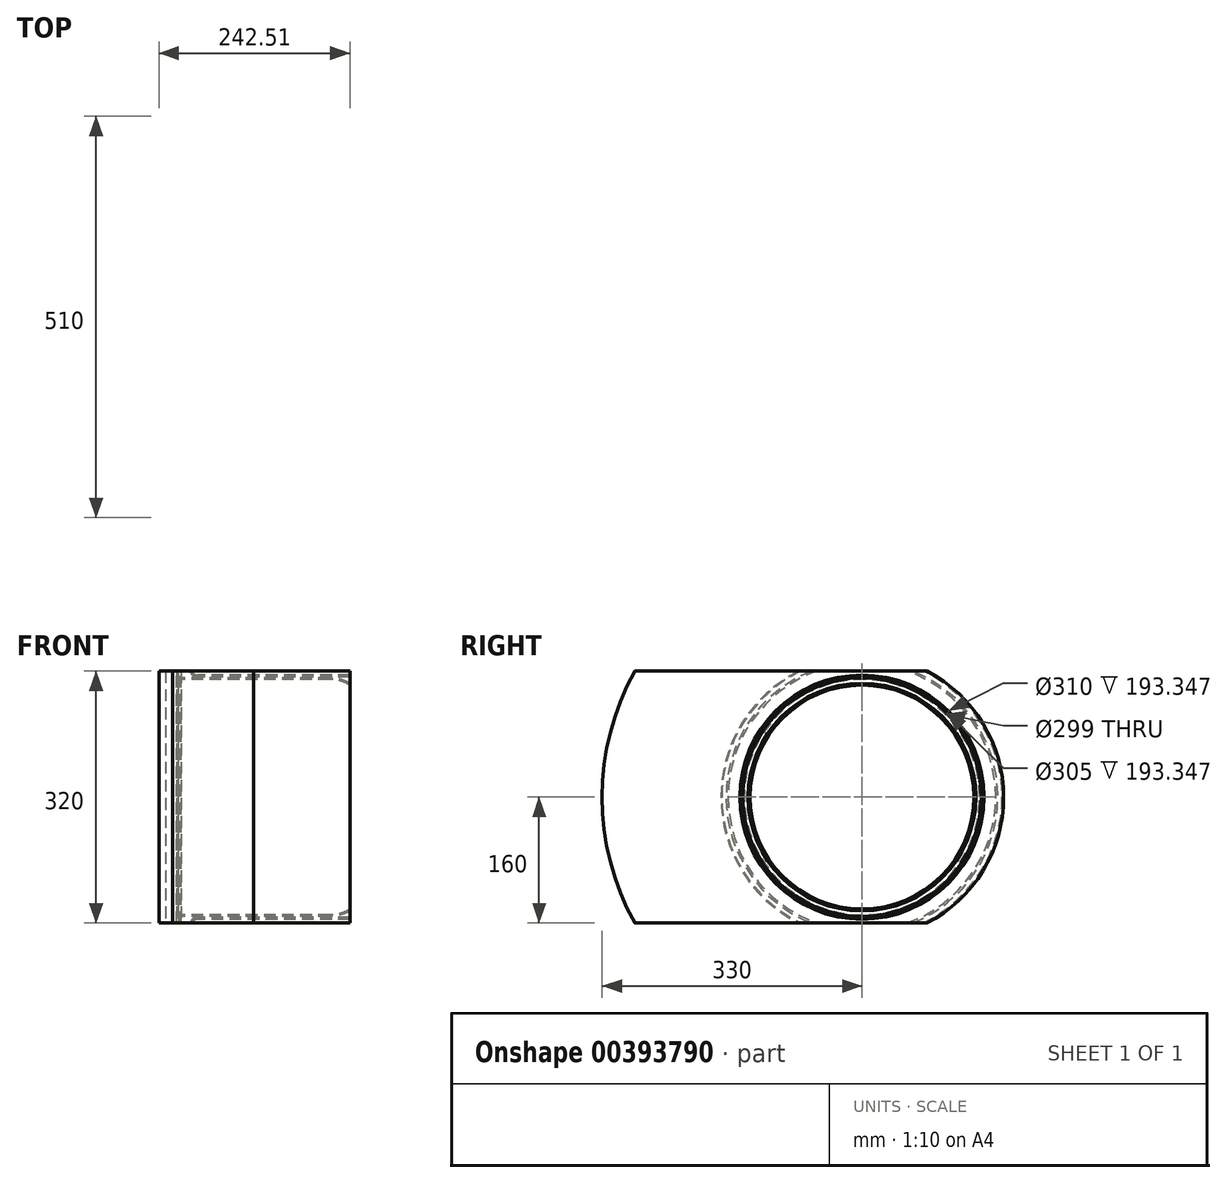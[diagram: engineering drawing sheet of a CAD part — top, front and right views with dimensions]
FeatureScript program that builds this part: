
annotation { "Feature Type Name" : "Feature", "Feature Type Description" : "" }
export const myFeature = defineFeature(function(context is Context, id is Id, definition is map)
    precondition{}
    {
        {
            var Q0;
            Q0=qCreatedBy(makeId("Front.planeOp"),FACE);
            var sketch = newSketch(context, id + "F0", { "sketchPlane" : qUnion([Q0])});
            skLineSegment(sketch, "E0", {"start": v(83.6, 147.98) * mm, "end": v(98.28, 137.71) * mm});
            skLineSegment(sketch, "E1", {"start": v(106.88, 135) * mm, "end": v(107.42, 135) * mm});
            skLineSegment(sketch, "E2", {"start": v(116.02, 137.71) * mm, "end": v(130.7, 147.98) * mm});
            skLineSegment(sketch, "E3", {"start": v(145.03, 152.5) * mm, "end": v(193.35, 152.5) * mm});
            skLineSegment(sketch, "E4", {"start": v(211.47, 170) * mm, "end": v(213.15, 170) * mm});
            skLineSegment(sketch, "E5", {"start": v(217.15, 174) * mm, "end": v(217.15, 178) * mm});
            skLineSegment(sketch, "E6", {"start": v(-211.47, 170) * mm, "end": v(-213.15, 170) * mm});
            skLineSegment(sketch, "E7", {"start": v(-217.15, 174) * mm, "end": v(-217.15, 178) * mm});
            skLineSegment(sketch, "E8", {"start": v(-193.35, 152.5) * mm, "end": v(69.27, 152.5) * mm});
            skLineSegment(sketch, "E9", {"start": v(-208, 167.98) * mm, "end": v(-202.03, 157.54) * mm});
            skLineSegment(sketch, "E10", {"start": v(202.03, 157.54) * mm, "end": v(208, 167.98) * mm});
            skPoint(sketch, "E11.visualSharp", {"position": v(217.15, 170) * mm});
            skArc(sketch, "E11.filletArc", {"start": v(213.15, 170) * mm, "mid": v(215.98, 171.17) * mm, "end": v(217.15, 174) * mm});
            skPoint(sketch, "E12.visualSharp", {"position": v(-217.15, 170) * mm});
            skArc(sketch, "E12.filletArc", {"start": v(-217.15, 174) * mm, "mid": v(-215.98, 171.17) * mm, "end": v(-213.15, 170) * mm});
            skPoint(sketch, "E13.visualSharp", {"position": v(-199.15, 152.5) * mm});
            skArc(sketch, "E13.filletArc", {"start": v(-202.03, 157.54) * mm, "mid": v(-198.37, 153.85) * mm, "end": v(-193.35, 152.5) * mm});
            skPoint(sketch, "E14.visualSharp", {"position": v(199.15, 152.5) * mm});
            skArc(sketch, "E14.filletArc", {"start": v(193.35, 152.5) * mm, "mid": v(198.37, 153.85) * mm, "end": v(202.03, 157.54) * mm});
            skPoint(sketch, "E15.visualSharp", {"position": v(-209.15, 170) * mm});
            skArc(sketch, "E15.filletArc", {"start": v(-208, 167.98) * mm, "mid": v(-209.46, 169.46) * mm, "end": v(-211.47, 170) * mm});
            skPoint(sketch, "E16.visualSharp", {"position": v(209.15, 170) * mm});
            skArc(sketch, "E16.filletArc", {"start": v(211.47, 170) * mm, "mid": v(209.46, 169.46) * mm, "end": v(208, 167.98) * mm});
            skPoint(sketch, "E17.visualSharp", {"position": v(77.15, 152.5) * mm});
            skArc(sketch, "E17.filletArc", {"start": v(83.6, 147.98) * mm, "mid": v(76.79, 151.34) * mm, "end": v(69.27, 152.5) * mm});
            skPoint(sketch, "E18.visualSharp", {"position": v(137.15, 152.5) * mm});
            skArc(sketch, "E18.filletArc", {"start": v(145.03, 152.5) * mm, "mid": v(137.51, 151.34) * mm, "end": v(130.7, 147.98) * mm});
            skPoint(sketch, "E19.visualSharp", {"position": v(112.15, 135) * mm});
            skArc(sketch, "E19.filletArc", {"start": v(107.42, 135) * mm, "mid": v(111.93, 135.7) * mm, "end": v(116.02, 137.71) * mm});
            skPoint(sketch, "E20.visualSharp", {"position": v(102.15, 135) * mm});
            skArc(sketch, "E20.filletArc", {"start": v(98.28, 137.71) * mm, "mid": v(102.37, 135.7) * mm, "end": v(106.88, 135) * mm});
            skLineSegment(sketch, "E21.0", {"start": v(214.65, 174) * mm, "end": v(214.65, 178) * mm});
            skArc(sketch, "E21.1", {"start": v(213.15, 172.5) * mm, "mid": v(214.21, 172.94) * mm, "end": v(214.65, 174) * mm});
            skLineSegment(sketch, "E21.2", {"start": v(211.47, 172.5) * mm, "end": v(213.15, 172.5) * mm});
            skArc(sketch, "E21.3", {"start": v(211.47, 172.5) * mm, "mid": v(208.2, 171.62) * mm, "end": v(205.83, 169.22) * mm});
            skLineSegment(sketch, "E21.4", {"start": v(199.86, 158.78) * mm, "end": v(205.83, 169.22) * mm});
            skArc(sketch, "E21.5", {"start": v(193.35, 155) * mm, "mid": v(197.11, 156.01) * mm, "end": v(199.86, 158.78) * mm});
            skLineSegment(sketch, "E21.6", {"start": v(145.03, 155) * mm, "end": v(193.35, 155) * mm});
            skArc(sketch, "E21.7", {"start": v(145.03, 155) * mm, "mid": v(136.76, 153.73) * mm, "end": v(129.26, 150.03) * mm});
            skLineSegment(sketch, "E21.8", {"start": v(114.59, 139.76) * mm, "end": v(129.26, 150.03) * mm});
            skArc(sketch, "E21.9", {"start": v(107.42, 137.5) * mm, "mid": v(111.18, 138.08) * mm, "end": v(114.59, 139.76) * mm});
            skLineSegment(sketch, "E21.10", {"start": v(106.88, 137.5) * mm, "end": v(107.42, 137.5) * mm});
            skArc(sketch, "E21.11", {"start": v(-205.83, 169.22) * mm, "mid": v(-208.2, 171.62) * mm, "end": v(-211.47, 172.5) * mm});
            skLineSegment(sketch, "E21.12", {"start": v(-211.47, 172.5) * mm, "end": v(-213.15, 172.5) * mm});
            skArc(sketch, "E21.13", {"start": v(-214.65, 174) * mm, "mid": v(-214.21, 172.94) * mm, "end": v(-213.15, 172.5) * mm});
            skLineSegment(sketch, "E21.14", {"start": v(-214.65, 174) * mm, "end": v(-214.65, 178) * mm});
            skLineSegment(sketch, "E21.15", {"start": v(-205.83, 169.22) * mm, "end": v(-199.86, 158.78) * mm});
            skArc(sketch, "E21.16", {"start": v(-199.86, 158.78) * mm, "mid": v(-197.11, 156.01) * mm, "end": v(-193.35, 155) * mm});
            skLineSegment(sketch, "E21.17", {"start": v(-193.35, 155) * mm, "end": v(69.27, 155) * mm});
            skArc(sketch, "E21.18", {"start": v(85.04, 150.03) * mm, "mid": v(77.54, 153.73) * mm, "end": v(69.27, 155) * mm});
            skLineSegment(sketch, "E21.19", {"start": v(85.04, 150.03) * mm, "end": v(99.71, 139.76) * mm});
            skArc(sketch, "E21.20", {"start": v(99.71, 139.76) * mm, "mid": v(103.12, 138.08) * mm, "end": v(106.88, 137.5) * mm});
            skLineSegment(sketch, "E22", {"start": v(216.15, 179) * mm, "end": v(215.65, 179) * mm});
            skLineSegment(sketch, "E23", {"start": v(-216.15, 179) * mm, "end": v(-215.65, 179) * mm});
            skPoint(sketch, "E24.visualSharp", {"position": v(-217.15, 179) * mm});
            skArc(sketch, "E24.filletArc", {"start": v(-216.15, 179) * mm, "mid": v(-216.86, 178.7) * mm, "end": v(-217.15, 178) * mm});
            skPoint(sketch, "E25.visualSharp", {"position": v(-214.65, 179) * mm});
            skArc(sketch, "E25.filletArc", {"start": v(-214.65, 178) * mm, "mid": v(-214.94, 178.7) * mm, "end": v(-215.65, 179) * mm});
            skPoint(sketch, "E26.visualSharp", {"position": v(214.65, 179) * mm});
            skArc(sketch, "E26.filletArc", {"start": v(215.65, 179) * mm, "mid": v(214.94, 178.7) * mm, "end": v(214.65, 178) * mm});
            skPoint(sketch, "E27.visualSharp", {"position": v(217.15, 179) * mm});
            skArc(sketch, "E27.filletArc", {"start": v(217.15, 178) * mm, "mid": v(216.86, 178.7) * mm, "end": v(216.15, 179) * mm});
            skLineSegment(sketch, "E28", {"start": v(-337.15, 0) * mm, "end": v(333.32, 0) * mm, "construction": true});
            skLineSegment(sketch, "E29", {"start": v(116.98, 138.38) * mm, "end": v(130.24, 88.88) * mm});
            skArc(sketch, "E30", {"start": v(130.24, 88.88) * mm, "mid": v(132.8, 76.05) * mm, "end": v(133.65, 63) * mm});
            skLineSegment(sketch, "E31", {"start": v(133.65, 63) * mm, "end": v(133.65, 94.03) * mm, "construction": true});
            skLineSegment(sketch, "E32", {"start": v(102.44, 48) * mm, "end": v(95.85, 48) * mm});
            skArc(sketch, "E33", {"start": v(95.85, 48) * mm, "mid": v(85.24, 52.4) * mm, "end": v(80.85, 63) * mm});
            skArc(sketch, "E34", {"start": v(80.85, 63) * mm, "mid": v(81.7, 76.05) * mm, "end": v(84.26, 88.88) * mm});
            skLineSegment(sketch, "E35", {"start": v(80.85, 63) * mm, "end": v(80.85, 94.03) * mm, "construction": true});
            skLineSegment(sketch, "E36", {"start": v(84.26, 88.88) * mm, "end": v(97.49, 138.26) * mm});
            skLineSegment(sketch, "E37", {"start": v(112.44, 38) * mm, "end": v(112.44, 38) * mm});
            skLineSegment(sketch, "E38", {"start": v(112.44, 38) * mm, "end": v(117.44, 38) * mm});
            skLineSegment(sketch, "E39", {"start": v(117.44, 38) * mm, "end": v(127.44, 48) * mm});
            skPoint(sketch, "E40.visualSharp", {"position": v(112.44, 48) * mm});
            skArc(sketch, "E40.filletArc", {"start": v(112.44, 38) * mm, "mid": v(109.5, 45.07) * mm, "end": v(102.44, 48) * mm});
            skArc(sketch, "E41", {"start": v(133.65, 63) * mm, "mid": v(132.04, 54.88) * mm, "end": v(127.44, 48) * mm});
            skFitSpline(sketch, "E42", {"points": [v(214.65, 178) * mm, v(214.82, 183.89) * mm, v(219.95, 211.54) * mm, v(223.88, 264.09) * mm, v(205.74, 304.9) * mm, v(202.5, 318.64) * mm], "startDerivative": vector(0, 87.75) * mm, "endDerivative": vector(0, 127.75) * mm});
            skLineSegment(sketch, "E43", {"start": v(202.5, 318.64) * mm, "end": v(202.5, 231.81) * mm, "construction": true});
            skArc(sketch, "E44.filletArc", {"start": v(204.62, 307.16) * mm, "mid": v(199.88, 313.65) * mm, "end": v(192.96, 317.75) * mm});
            skArc(sketch, "E45", {"start": v(192.96, 317.75) * mm, "mid": v(170.42, 324.1) * mm, "end": v(147.29, 327.75) * mm});
            skLineSegment(sketch, "E46", {"start": v(-25.36, 151.5) * mm, "end": v(-216.15, 151.5) * mm});
            skFitSpline(sketch, "E47", {"points": [v(-218.15, 178) * mm, v(-233.61, 240.25) * mm, v(-225.26, 324.61) * mm, v(-226.47, 330) * mm, v(-234.2, 316.72) * mm, v(-239.75, 236.6) * mm, v(-220.15, 178) * mm], "startDerivative": vector(-1.84, 180.77) * mm, "endDerivative": vector(3.66, -186.13) * mm});
            skLineSegment(sketch, "E48", {"start": v(-220.15, 178) * mm, "end": v(-220.15, 0) * mm});
            skLineSegment(sketch, "E49", {"start": v(-220.15, 0) * mm, "end": v(-218.15, 0) * mm});
            skLineSegment(sketch, "E50", {"start": v(-218.15, 0) * mm, "end": v(-218.15, 147.5) * mm});
            skLineSegment(sketch, "E51", {"start": v(-216.15, 149.5) * mm, "end": v(-25.36, 149.5) * mm});
            skArc(sketch, "E52", {"start": v(-25.36, 151.5) * mm, "mid": v(-6.23, 147.7) * mm, "end": v(10, 136.86) * mm});
            skLineSegment(sketch, "E53", {"start": v(10, 136.86) * mm, "end": v(21.85, 125) * mm});
            skLineSegment(sketch, "E54", {"start": v(21.85, 125) * mm, "end": v(20.44, 123.59) * mm});
            skArc(sketch, "E55", {"start": v(-25.36, 149.5) * mm, "mid": v(-7, 145.85) * mm, "end": v(8.58, 135.44) * mm});
            skLineSegment(sketch, "E56", {"start": v(20.44, 123.59) * mm, "end": v(8.58, 135.44) * mm});
            skArc(sketch, "E57", {"start": v(-218.15, 147.5) * mm, "mid": v(-217.56, 148.91) * mm, "end": v(-216.15, 149.5) * mm});
            skLineSegment(sketch, "E58", {"start": v(-218.15, 178) * mm, "end": v(-218.15, 153.5) * mm});
            skArc(sketch, "E59", {"start": v(-218.15, 153.5) * mm, "mid": v(-217.56, 152.09) * mm, "end": v(-216.15, 151.5) * mm});
            skLineSegment(sketch, "E60", {"start": v(-337.15, 330) * mm, "end": v(-217.15, 330) * mm, "construction": true});
            skLineSegment(sketch, "E61", {"start": v(-337.15, 330) * mm, "end": v(-337.15, 0) * mm, "construction": true});
            skArc(sketch, "E62", {"start": v(147.29, 327.75) * mm, "mid": v(73.73, 333.19) * mm, "end": v(0, 335) * mm});
            skLineSegment(sketch, "E63", {"start": v(0, 335) * mm, "end": v(-337.15, 335) * mm, "construction": true});
            skLineSegment(sketch, "E64", {"start": v(232.5, 335) * mm, "end": v(232.5, 174) * mm, "construction": true});
            skLineSegment(sketch, "E65", {"start": v(225, 335) * mm, "end": v(225, 174) * mm, "construction": true});
            skFitSpline(sketch, "E66.MirrorCS", {"points": [v(-214.65, 178) * mm, v(-214.82, 183.89) * mm, v(-219.95, 211.54) * mm, v(-223.88, 264.09) * mm, v(-205.74, 304.9) * mm, v(-202.5, 318.64) * mm], "startDerivative": vector(0, 87.75) * mm, "endDerivative": vector(0, 127.75) * mm});
            skArc(sketch, "E67.MirrorCS", {"start": v(-204.62, 307.16) * mm, "mid": v(-199.88, 313.65) * mm, "end": v(-192.96, 317.75) * mm});
            skArc(sketch, "E68.MirrorCS", {"start": v(-192.96, 317.75) * mm, "mid": v(-170.42, 324.1) * mm, "end": v(-147.29, 327.75) * mm});
            skArc(sketch, "E69.MirrorCS", {"start": v(-147.29, 327.75) * mm, "mid": v(-73.73, 333.19) * mm, "end": v(0, 335) * mm});
            skSolve(sketch);
        }
        {
            var Q0;
            Q0=qCreatedBy(makeId("Right.planeOp"),FACE);
            var sketch = newSketch(context, id + "F1", { "sketchPlane" : qUnion([Q0])});
            skArc(sketch, "E70", {"start": v(-29.75, 149.57) * mm, "mid": v(0, 152.5) * mm, "end": v(29.75, 149.57) * mm, "construction": true});
            skLineSegment(sketch, "E71", {"start": v(-29.75, 149.57) * mm, "end": v(0, 0) * mm, "construction": true});
            skLineSegment(sketch, "E72", {"start": v(29.75, 149.57) * mm, "end": v(0, 0) * mm, "construction": true});
            skArc(sketch, "E73", {"start": v(10.34, 51.98) * mm, "mid": v(0, 53) * mm, "end": v(-10.34, 51.98) * mm, "construction": true});
            skLineSegment(sketch, "E74", {"start": v(0, 0) * mm, "end": v(-34.81, 197.43) * mm, "construction": true});
            skLineSegment(sketch, "E75", {"start": v(0, 0) * mm, "end": v(34.81, 197.43) * mm, "construction": true});
            skArc(sketch, "E76", {"start": v(26.48, 150.18) * mm, "mid": v(0, 152.5) * mm, "end": v(-26.48, 150.18) * mm});
            skLineSegment(sketch, "E77", {"start": v(0, 0) * mm, "end": v(19.74, 187.83) * mm, "construction": true});
            skLineSegment(sketch, "E78", {"start": v(0, 0) * mm, "end": v(-19.74, 187.83) * mm, "construction": true});
            skLineSegment(sketch, "E79", {"start": v(-6.78, 58.48) * mm, "end": v(-26.48, 150.18) * mm});
            skLineSegment(sketch, "E80", {"start": v(6.78, 58.48) * mm, "end": v(26.48, 150.18) * mm});
            skPoint(sketch, "E81.visualSharp", {"position": v(-5.54, 52.7) * mm});
            skArc(sketch, "E81.filletArc", {"start": v(-6.78, 58.48) * mm, "mid": v(-4.36, 54.54) * mm, "end": v(0, 53) * mm});
            skPoint(sketch, "E82.visualSharp", {"position": v(5.54, 52.7) * mm});
            skArc(sketch, "E82.filletArc", {"start": v(0, 53) * mm, "mid": v(4.36, 54.54) * mm, "end": v(6.78, 58.48) * mm});
            skSolve(sketch);
        }
        {
            var Q0;
            Q0=qCreatedBy(makeId("Right.planeOp"),FACE);
            var sketch = newSketch(context, id + "F2", { "sketchPlane" : qUnion([Q0])});
            skLineSegment(sketch, "E83", {"start": v(-288.62, 160) * mm, "end": v(82.46, 160) * mm});
            skLineSegment(sketch, "E84", {"start": v(-288.62, -160) * mm, "end": v(82.46, -160) * mm});
            skArc(sketch, "E85", {"start": v(82.46, 160) * mm, "mid": v(180, 0) * mm, "end": v(82.46, -160) * mm});
            skArc(sketch, "E86", {"start": v(-288.62, 160) * mm, "mid": v(-330, 0) * mm, "end": v(-288.62, -160) * mm});
            skSolve(sketch);
        }
        {
            var Q0;
            Q0=makeQuery(id+"F0.imprint","IMPRINT",FACE,{"disambiguationData":[TD([[makeQuery(id+"F0.imprint","IMPRINT",EDGE,{"derivedFrom":sQuery(id+"F0.wireOp",EDGE,"E3")}),1.0]])]});
            var Q1;
            Q1=sQuery(id+"F0.wireOp",EDGE,"E28");
            revolve(context, id + "F3", {"entities" : qUnion([Q0]), "axis" : qUnion([Q1]), "revolveType" : RevolveType.FULL});
        }
        {
            var Q0;
            Q0=makeQuery(id+"F0.imprint","IMPRINT",FACE,{"disambiguationData":[TD([[makeQuery(id+"F0.imprint","IMPRINT",EDGE,{"derivedFrom":sQuery(id+"F0.wireOp",EDGE,"E1")}),-1.0]])]});
            var Q1;
            Q1=sQuery(id+"F0.wireOp",EDGE,"E28");
            revolve(context, id + "F4", {"entities" : qUnion([Q0]), "axis" : qUnion([Q1]), "revolveType" : RevolveType.FULL});
        }
        {
            var Q0;
            Q0=makeQuery(id+"F1.imprint","IMPRINT",FACE,{"disambiguationData":[TD([[makeQuery(id+"F1.imprint","IMPRINT",EDGE,{"derivedFrom":sQuery(id+"F1.wireOp",EDGE,"E76")}),1.0]])]});
            extrude(context, id + "F5", {"entities" : qUnion([Q0]), "operationType" : NewBodyOperationType.REMOVE, "endBound" : BoundingType.THROUGH_ALL, "oppositeDirection" : true, "depth" : 25 * mm, "hasSecondDirection" : true, "secondDirectionBound" : SecondDirectionBoundingType.THROUGH_ALL, "secondDirectionOppositeDirection" : false, "secondDirectionDepth" : 25 * mm});
        }
        {
            var Q0;
            Q0=makeQuery(id+"F5.boolean.opBoolean","INTERSECT",EDGE,{"derivedFrom":[makeQuery(id+"F4.opRevolve","SWEPT_FACE",FACE,{"disambiguationData":[OSD([sQuery(id+"F0.wireOp",EDGE,"E34")])]}),makeQuery(id+"F5.opExtrude","SWEPT_FACE",FACE,{"disambiguationData":[OSD([sQuery(id+"F1.wireOp",EDGE,"E80")])]})]});
            var Q1;
            Q1=makeQuery(id+"F1MoAnU7Y2teXVl_2.1.F5.boolean.opBoolean","INTERSECT",EDGE,{"derivedFrom":[makeQuery(id+"F4.opRevolve","SWEPT_FACE",FACE,{"disambiguationData":[OSD([sQuery(id+"F0.wireOp",EDGE,"E34")])]}),makeQuery(id+"F1MoAnU7Y2teXVl_2.1.F5.opExtrude","SWEPT_FACE",FACE,{"disambiguationData":[OSD([sQuery(id+"F1.wireOp",EDGE,"E80")])]})]});
            var Q2;
            {var subQ0=sQuery(id+"F1.wireOp",EDGE,"E80");Q2=makeQuery(id+"F1MoAnU7Y2teXVl_2.2.F5.boolean.opBoolean","INTERSECT",EDGE,{"derivedFrom":[makeQuery(id+"F1MoAnU7Y2teXVl_2.1.F5.boolean.opBoolean","SPLIT",FACE,{"disambiguationData":[TD([makeQuery(id+"F5.boolean.opBoolean","COPY",FACE,{"derivedFrom":makeQuery(id+"F5.opExtrude","SWEPT_FACE",FACE,{"disambiguationData":[OSD([subQ0])]})})])],"derivedFrom":makeQuery(id+"F4.opRevolve","SWEPT_FACE",FACE,{"disambiguationData":[OSD([sQuery(id+"F0.wireOp",EDGE,"E34")])]})}),makeQuery(id+"F1MoAnU7Y2teXVl_2.2.F5.opExtrude","SWEPT_FACE",FACE,{"disambiguationData":[OSD([subQ0])]})]});}
            var Q3;
            {var subQ0=sQuery(id+"F1.wireOp",EDGE,"E80");var subQ3=makeQuery(id+"F5.boolean.opBoolean","COPY",FACE,{"derivedFrom":makeQuery(id+"F5.opExtrude","SWEPT_FACE",FACE,{"disambiguationData":[OSD([subQ0])]})});Q3=makeQuery(id+"F1MoAnU7Y2teXVl_2.3.F5.boolean.opBoolean","INTERSECT",EDGE,{"derivedFrom":[makeQuery(id+"F1MoAnU7Y2teXVl_2.2.F5.boolean.opBoolean","SPLIT",FACE,{"disambiguationData":[TD([subQ3])],"derivedFrom":makeQuery(id+"F1MoAnU7Y2teXVl_2.1.F5.boolean.opBoolean","SPLIT",FACE,{"disambiguationData":[TD([subQ3])],"derivedFrom":makeQuery(id+"F4.opRevolve","SWEPT_FACE",FACE,{"disambiguationData":[OSD([sQuery(id+"F0.wireOp",EDGE,"E34")])]})})}),makeQuery(id+"F1MoAnU7Y2teXVl_2.3.F5.opExtrude","SWEPT_FACE",FACE,{"disambiguationData":[OSD([subQ0])]})]});}
            var Q4;
            {var subQ0=sQuery(id+"F1.wireOp",EDGE,"E80");var subQ3=makeQuery(id+"F5.boolean.opBoolean","COPY",FACE,{"derivedFrom":makeQuery(id+"F5.opExtrude","SWEPT_FACE",FACE,{"disambiguationData":[OSD([subQ0])]})});Q4=makeQuery(id+"F1MoAnU7Y2teXVl_2.4.F5.boolean.opBoolean","INTERSECT",EDGE,{"derivedFrom":[makeQuery(id+"F1MoAnU7Y2teXVl_2.3.F5.boolean.opBoolean","SPLIT",FACE,{"disambiguationData":[TD([subQ3])],"derivedFrom":makeQuery(id+"F1MoAnU7Y2teXVl_2.2.F5.boolean.opBoolean","SPLIT",FACE,{"disambiguationData":[TD([subQ3])],"derivedFrom":makeQuery(id+"F1MoAnU7Y2teXVl_2.1.F5.boolean.opBoolean","SPLIT",FACE,{"disambiguationData":[TD([subQ3])],"derivedFrom":makeQuery(id+"F4.opRevolve","SWEPT_FACE",FACE,{"disambiguationData":[OSD([sQuery(id+"F0.wireOp",EDGE,"E34")])]})})})}),makeQuery(id+"F1MoAnU7Y2teXVl_2.4.F5.opExtrude","SWEPT_FACE",FACE,{"disambiguationData":[OSD([subQ0])]})]});}
            var Q5;
            {var subQ0=sQuery(id+"F1.wireOp",EDGE,"E80");var subQ3=makeQuery(id+"F5.boolean.opBoolean","COPY",FACE,{"derivedFrom":makeQuery(id+"F5.opExtrude","SWEPT_FACE",FACE,{"disambiguationData":[OSD([subQ0])]})});Q5=makeQuery(id+"F1MoAnU7Y2teXVl_2.5.F5.boolean.opBoolean","INTERSECT",EDGE,{"derivedFrom":[makeQuery(id+"F1MoAnU7Y2teXVl_2.4.F5.boolean.opBoolean","SPLIT",FACE,{"disambiguationData":[TD([subQ3])],"derivedFrom":makeQuery(id+"F1MoAnU7Y2teXVl_2.3.F5.boolean.opBoolean","SPLIT",FACE,{"disambiguationData":[TD([subQ3])],"derivedFrom":makeQuery(id+"F1MoAnU7Y2teXVl_2.2.F5.boolean.opBoolean","SPLIT",FACE,{"disambiguationData":[TD([subQ3])],"derivedFrom":makeQuery(id+"F1MoAnU7Y2teXVl_2.1.F5.boolean.opBoolean","SPLIT",FACE,{"disambiguationData":[TD([subQ3])],"derivedFrom":makeQuery(id+"F4.opRevolve","SWEPT_FACE",FACE,{"disambiguationData":[OSD([sQuery(id+"F0.wireOp",EDGE,"E34")])]})})})})}),makeQuery(id+"F1MoAnU7Y2teXVl_2.5.F5.opExtrude","SWEPT_FACE",FACE,{"disambiguationData":[OSD([subQ0])]})]});}
            var Q6;
            {var subQ0=sQuery(id+"F1.wireOp",EDGE,"E80");var subQ4=makeQuery(id+"F5.boolean.opBoolean","COPY",FACE,{"derivedFrom":makeQuery(id+"F5.opExtrude","SWEPT_FACE",FACE,{"disambiguationData":[OSD([subQ0])]})});Q6=makeQuery(id+"F1MoAnU7Y2teXVl_2.6.F5.boolean.opBoolean","INTERSECT",EDGE,{"derivedFrom":[makeQuery(id+"F1MoAnU7Y2teXVl_2.5.F5.boolean.opBoolean","SPLIT",FACE,{"disambiguationData":[TD([subQ4])],"derivedFrom":makeQuery(id+"F1MoAnU7Y2teXVl_2.4.F5.boolean.opBoolean","SPLIT",FACE,{"disambiguationData":[TD([subQ4])],"derivedFrom":makeQuery(id+"F1MoAnU7Y2teXVl_2.3.F5.boolean.opBoolean","SPLIT",FACE,{"disambiguationData":[TD([subQ4])],"derivedFrom":makeQuery(id+"F1MoAnU7Y2teXVl_2.2.F5.boolean.opBoolean","SPLIT",FACE,{"disambiguationData":[TD([subQ4])],"derivedFrom":makeQuery(id+"F1MoAnU7Y2teXVl_2.1.F5.boolean.opBoolean","SPLIT",FACE,{"disambiguationData":[TD([subQ4])],"derivedFrom":makeQuery(id+"F4.opRevolve","SWEPT_FACE",FACE,{"disambiguationData":[OSD([sQuery(id+"F0.wireOp",EDGE,"E34")])]})})})})})}),makeQuery(id+"F1MoAnU7Y2teXVl_2.6.F5.opExtrude","SWEPT_FACE",FACE,{"disambiguationData":[OSD([subQ0])]})]});}
            var Q7;
            {var subQ0=sQuery(id+"F1.wireOp",EDGE,"E80");var subQ3=makeQuery(id+"F5.boolean.opBoolean","COPY",FACE,{"derivedFrom":makeQuery(id+"F5.opExtrude","SWEPT_FACE",FACE,{"disambiguationData":[OSD([subQ0])]})});Q7=makeQuery(id+"F1MoAnU7Y2teXVl_2.7.F5.boolean.opBoolean","INTERSECT",EDGE,{"derivedFrom":[makeQuery(id+"F1MoAnU7Y2teXVl_2.6.F5.boolean.opBoolean","SPLIT",FACE,{"disambiguationData":[TD([subQ3])],"derivedFrom":makeQuery(id+"F1MoAnU7Y2teXVl_2.5.F5.boolean.opBoolean","SPLIT",FACE,{"disambiguationData":[TD([subQ3])],"derivedFrom":makeQuery(id+"F1MoAnU7Y2teXVl_2.4.F5.boolean.opBoolean","SPLIT",FACE,{"disambiguationData":[TD([subQ3])],"derivedFrom":makeQuery(id+"F1MoAnU7Y2teXVl_2.3.F5.boolean.opBoolean","SPLIT",FACE,{"disambiguationData":[TD([subQ3])],"derivedFrom":makeQuery(id+"F1MoAnU7Y2teXVl_2.2.F5.boolean.opBoolean","SPLIT",FACE,{"disambiguationData":[TD([subQ3])],"derivedFrom":makeQuery(id+"F1MoAnU7Y2teXVl_2.1.F5.boolean.opBoolean","SPLIT",FACE,{"disambiguationData":[TD([subQ3])],"derivedFrom":makeQuery(id+"F4.opRevolve","SWEPT_FACE",FACE,{"disambiguationData":[OSD([sQuery(id+"F0.wireOp",EDGE,"E34")])]})})})})})})}),makeQuery(id+"F1MoAnU7Y2teXVl_2.7.F5.opExtrude","SWEPT_FACE",FACE,{"disambiguationData":[OSD([subQ0])]})]});}
            var Q8;
            {var subQ0=sQuery(id+"F1.wireOp",EDGE,"E80");var subQ3=makeQuery(id+"F5.boolean.opBoolean","COPY",FACE,{"derivedFrom":makeQuery(id+"F5.opExtrude","SWEPT_FACE",FACE,{"disambiguationData":[OSD([subQ0])]})});Q8=makeQuery(id+"F1MoAnU7Y2teXVl_2.8.F5.boolean.opBoolean","INTERSECT",EDGE,{"derivedFrom":[makeQuery(id+"F1MoAnU7Y2teXVl_2.7.F5.boolean.opBoolean","SPLIT",FACE,{"disambiguationData":[TD([subQ3])],"derivedFrom":makeQuery(id+"F1MoAnU7Y2teXVl_2.6.F5.boolean.opBoolean","SPLIT",FACE,{"disambiguationData":[TD([subQ3])],"derivedFrom":makeQuery(id+"F1MoAnU7Y2teXVl_2.5.F5.boolean.opBoolean","SPLIT",FACE,{"disambiguationData":[TD([subQ3])],"derivedFrom":makeQuery(id+"F1MoAnU7Y2teXVl_2.4.F5.boolean.opBoolean","SPLIT",FACE,{"disambiguationData":[TD([subQ3])],"derivedFrom":makeQuery(id+"F1MoAnU7Y2teXVl_2.3.F5.boolean.opBoolean","SPLIT",FACE,{"disambiguationData":[TD([subQ3])],"derivedFrom":makeQuery(id+"F1MoAnU7Y2teXVl_2.2.F5.boolean.opBoolean","SPLIT",FACE,{"disambiguationData":[TD([subQ3])],"derivedFrom":makeQuery(id+"F1MoAnU7Y2teXVl_2.1.F5.boolean.opBoolean","SPLIT",FACE,{"disambiguationData":[TD([subQ3])],"derivedFrom":makeQuery(id+"F4.opRevolve","SWEPT_FACE",FACE,{"disambiguationData":[OSD([sQuery(id+"F0.wireOp",EDGE,"E34")])]})})})})})})})}),makeQuery(id+"F1MoAnU7Y2teXVl_2.8.F5.opExtrude","SWEPT_FACE",FACE,{"disambiguationData":[OSD([subQ0])]})]});}
            var Q9;
            {var subQ0=sQuery(id+"F1.wireOp",EDGE,"E80");var subQ3=makeQuery(id+"F5.boolean.opBoolean","COPY",FACE,{"derivedFrom":makeQuery(id+"F5.opExtrude","SWEPT_FACE",FACE,{"disambiguationData":[OSD([subQ0])]})});Q9=makeQuery(id+"F1MoAnU7Y2teXVl_2.9.F5.boolean.opBoolean","INTERSECT",EDGE,{"derivedFrom":[makeQuery(id+"F1MoAnU7Y2teXVl_2.8.F5.boolean.opBoolean","SPLIT",FACE,{"disambiguationData":[TD([subQ3])],"derivedFrom":makeQuery(id+"F1MoAnU7Y2teXVl_2.7.F5.boolean.opBoolean","SPLIT",FACE,{"disambiguationData":[TD([subQ3])],"derivedFrom":makeQuery(id+"F1MoAnU7Y2teXVl_2.6.F5.boolean.opBoolean","SPLIT",FACE,{"disambiguationData":[TD([subQ3])],"derivedFrom":makeQuery(id+"F1MoAnU7Y2teXVl_2.5.F5.boolean.opBoolean","SPLIT",FACE,{"disambiguationData":[TD([subQ3])],"derivedFrom":makeQuery(id+"F1MoAnU7Y2teXVl_2.4.F5.boolean.opBoolean","SPLIT",FACE,{"disambiguationData":[TD([subQ3])],"derivedFrom":makeQuery(id+"F1MoAnU7Y2teXVl_2.3.F5.boolean.opBoolean","SPLIT",FACE,{"disambiguationData":[TD([subQ3])],"derivedFrom":makeQuery(id+"F1MoAnU7Y2teXVl_2.2.F5.boolean.opBoolean","SPLIT",FACE,{"disambiguationData":[TD([subQ3])],"derivedFrom":makeQuery(id+"F1MoAnU7Y2teXVl_2.1.F5.boolean.opBoolean","SPLIT",FACE,{"disambiguationData":[TD([subQ3])],"derivedFrom":makeQuery(id+"F4.opRevolve","SWEPT_FACE",FACE,{"disambiguationData":[OSD([sQuery(id+"F0.wireOp",EDGE,"E34")])]})})})})})})})})}),makeQuery(id+"F1MoAnU7Y2teXVl_2.9.F5.opExtrude","SWEPT_FACE",FACE,{"disambiguationData":[OSD([subQ0])]})]});}
            var Q10;
            {var subQ0=sQuery(id+"F1.wireOp",EDGE,"E80");var subQ4=makeQuery(id+"F5.boolean.opBoolean","COPY",FACE,{"derivedFrom":makeQuery(id+"F5.opExtrude","SWEPT_FACE",FACE,{"disambiguationData":[OSD([subQ0])]})});Q10=makeQuery(id+"F1MoAnU7Y2teXVl_2.10.F5.boolean.opBoolean","INTERSECT",EDGE,{"derivedFrom":[makeQuery(id+"F1MoAnU7Y2teXVl_2.9.F5.boolean.opBoolean","SPLIT",FACE,{"disambiguationData":[TD([subQ4])],"derivedFrom":makeQuery(id+"F1MoAnU7Y2teXVl_2.8.F5.boolean.opBoolean","SPLIT",FACE,{"disambiguationData":[TD([subQ4])],"derivedFrom":makeQuery(id+"F1MoAnU7Y2teXVl_2.7.F5.boolean.opBoolean","SPLIT",FACE,{"disambiguationData":[TD([subQ4])],"derivedFrom":makeQuery(id+"F1MoAnU7Y2teXVl_2.6.F5.boolean.opBoolean","SPLIT",FACE,{"disambiguationData":[TD([subQ4])],"derivedFrom":makeQuery(id+"F1MoAnU7Y2teXVl_2.5.F5.boolean.opBoolean","SPLIT",FACE,{"disambiguationData":[TD([subQ4])],"derivedFrom":makeQuery(id+"F1MoAnU7Y2teXVl_2.4.F5.boolean.opBoolean","SPLIT",FACE,{"disambiguationData":[TD([subQ4])],"derivedFrom":makeQuery(id+"F1MoAnU7Y2teXVl_2.3.F5.boolean.opBoolean","SPLIT",FACE,{"disambiguationData":[TD([subQ4])],"derivedFrom":makeQuery(id+"F1MoAnU7Y2teXVl_2.2.F5.boolean.opBoolean","SPLIT",FACE,{"disambiguationData":[TD([subQ4])],"derivedFrom":makeQuery(id+"F1MoAnU7Y2teXVl_2.1.F5.boolean.opBoolean","SPLIT",FACE,{"disambiguationData":[TD([subQ4])],"derivedFrom":makeQuery(id+"F4.opRevolve","SWEPT_FACE",FACE,{"disambiguationData":[OSD([sQuery(id+"F0.wireOp",EDGE,"E34")])]})})})})})})})})})}),makeQuery(id+"F1MoAnU7Y2teXVl_2.10.F5.opExtrude","SWEPT_FACE",FACE,{"disambiguationData":[OSD([subQ0])]})]});}
            var Q11;
            {var subQ0=sQuery(id+"F1.wireOp",EDGE,"E80");var subQ3=makeQuery(id+"F5.boolean.opBoolean","COPY",FACE,{"derivedFrom":makeQuery(id+"F5.opExtrude","SWEPT_FACE",FACE,{"disambiguationData":[OSD([subQ0])]})});Q11=makeQuery(id+"F1MoAnU7Y2teXVl_2.11.F5.boolean.opBoolean","INTERSECT",EDGE,{"derivedFrom":[makeQuery(id+"F1MoAnU7Y2teXVl_2.10.F5.boolean.opBoolean","SPLIT",FACE,{"disambiguationData":[TD([subQ3])],"derivedFrom":makeQuery(id+"F1MoAnU7Y2teXVl_2.9.F5.boolean.opBoolean","SPLIT",FACE,{"disambiguationData":[TD([subQ3])],"derivedFrom":makeQuery(id+"F1MoAnU7Y2teXVl_2.8.F5.boolean.opBoolean","SPLIT",FACE,{"disambiguationData":[TD([subQ3])],"derivedFrom":makeQuery(id+"F1MoAnU7Y2teXVl_2.7.F5.boolean.opBoolean","SPLIT",FACE,{"disambiguationData":[TD([subQ3])],"derivedFrom":makeQuery(id+"F1MoAnU7Y2teXVl_2.6.F5.boolean.opBoolean","SPLIT",FACE,{"disambiguationData":[TD([subQ3])],"derivedFrom":makeQuery(id+"F1MoAnU7Y2teXVl_2.5.F5.boolean.opBoolean","SPLIT",FACE,{"disambiguationData":[TD([subQ3])],"derivedFrom":makeQuery(id+"F1MoAnU7Y2teXVl_2.4.F5.boolean.opBoolean","SPLIT",FACE,{"disambiguationData":[TD([subQ3])],"derivedFrom":makeQuery(id+"F1MoAnU7Y2teXVl_2.3.F5.boolean.opBoolean","SPLIT",FACE,{"disambiguationData":[TD([subQ3])],"derivedFrom":makeQuery(id+"F1MoAnU7Y2teXVl_2.2.F5.boolean.opBoolean","SPLIT",FACE,{"disambiguationData":[TD([subQ3])],"derivedFrom":makeQuery(id+"F1MoAnU7Y2teXVl_2.1.F5.boolean.opBoolean","SPLIT",FACE,{"disambiguationData":[TD([subQ3])],"derivedFrom":makeQuery(id+"F4.opRevolve","SWEPT_FACE",FACE,{"disambiguationData":[OSD([sQuery(id+"F0.wireOp",EDGE,"E34")])]})})})})})})})})})})}),makeQuery(id+"F1MoAnU7Y2teXVl_2.11.F5.opExtrude","SWEPT_FACE",FACE,{"disambiguationData":[OSD([subQ0])]})]});}
            var Q12;
            {var subQ0=sQuery(id+"F1.wireOp",EDGE,"E80");var subQ3=makeQuery(id+"F5.boolean.opBoolean","COPY",FACE,{"derivedFrom":makeQuery(id+"F5.opExtrude","SWEPT_FACE",FACE,{"disambiguationData":[OSD([subQ0])]})});Q12=makeQuery(id+"F1MoAnU7Y2teXVl_2.12.F5.boolean.opBoolean","INTERSECT",EDGE,{"derivedFrom":[makeQuery(id+"F1MoAnU7Y2teXVl_2.11.F5.boolean.opBoolean","SPLIT",FACE,{"disambiguationData":[TD([subQ3])],"derivedFrom":makeQuery(id+"F1MoAnU7Y2teXVl_2.10.F5.boolean.opBoolean","SPLIT",FACE,{"disambiguationData":[TD([subQ3])],"derivedFrom":makeQuery(id+"F1MoAnU7Y2teXVl_2.9.F5.boolean.opBoolean","SPLIT",FACE,{"disambiguationData":[TD([subQ3])],"derivedFrom":makeQuery(id+"F1MoAnU7Y2teXVl_2.8.F5.boolean.opBoolean","SPLIT",FACE,{"disambiguationData":[TD([subQ3])],"derivedFrom":makeQuery(id+"F1MoAnU7Y2teXVl_2.7.F5.boolean.opBoolean","SPLIT",FACE,{"disambiguationData":[TD([subQ3])],"derivedFrom":makeQuery(id+"F1MoAnU7Y2teXVl_2.6.F5.boolean.opBoolean","SPLIT",FACE,{"disambiguationData":[TD([subQ3])],"derivedFrom":makeQuery(id+"F1MoAnU7Y2teXVl_2.5.F5.boolean.opBoolean","SPLIT",FACE,{"disambiguationData":[TD([subQ3])],"derivedFrom":makeQuery(id+"F1MoAnU7Y2teXVl_2.4.F5.boolean.opBoolean","SPLIT",FACE,{"disambiguationData":[TD([subQ3])],"derivedFrom":makeQuery(id+"F1MoAnU7Y2teXVl_2.3.F5.boolean.opBoolean","SPLIT",FACE,{"disambiguationData":[TD([subQ3])],"derivedFrom":makeQuery(id+"F1MoAnU7Y2teXVl_2.2.F5.boolean.opBoolean","SPLIT",FACE,{"disambiguationData":[TD([subQ3])],"derivedFrom":makeQuery(id+"F1MoAnU7Y2teXVl_2.1.F5.boolean.opBoolean","SPLIT",FACE,{"disambiguationData":[TD([subQ3])],"derivedFrom":makeQuery(id+"F4.opRevolve","SWEPT_FACE",FACE,{"disambiguationData":[OSD([sQuery(id+"F0.wireOp",EDGE,"E34")])]})})})})})})})})})})})}),makeQuery(id+"F1MoAnU7Y2teXVl_2.12.F5.opExtrude","SWEPT_FACE",FACE,{"disambiguationData":[OSD([subQ0])]})]});}
            var Q13;
            {var subQ0=sQuery(id+"F1.wireOp",EDGE,"E80");var subQ3=makeQuery(id+"F5.boolean.opBoolean","COPY",FACE,{"derivedFrom":makeQuery(id+"F5.opExtrude","SWEPT_FACE",FACE,{"disambiguationData":[OSD([subQ0])]})});Q13=makeQuery(id+"F1MoAnU7Y2teXVl_2.13.F5.boolean.opBoolean","INTERSECT",EDGE,{"derivedFrom":[makeQuery(id+"F1MoAnU7Y2teXVl_2.12.F5.boolean.opBoolean","SPLIT",FACE,{"disambiguationData":[TD([subQ3])],"derivedFrom":makeQuery(id+"F1MoAnU7Y2teXVl_2.11.F5.boolean.opBoolean","SPLIT",FACE,{"disambiguationData":[TD([subQ3])],"derivedFrom":makeQuery(id+"F1MoAnU7Y2teXVl_2.10.F5.boolean.opBoolean","SPLIT",FACE,{"disambiguationData":[TD([subQ3])],"derivedFrom":makeQuery(id+"F1MoAnU7Y2teXVl_2.9.F5.boolean.opBoolean","SPLIT",FACE,{"disambiguationData":[TD([subQ3])],"derivedFrom":makeQuery(id+"F1MoAnU7Y2teXVl_2.8.F5.boolean.opBoolean","SPLIT",FACE,{"disambiguationData":[TD([subQ3])],"derivedFrom":makeQuery(id+"F1MoAnU7Y2teXVl_2.7.F5.boolean.opBoolean","SPLIT",FACE,{"disambiguationData":[TD([subQ3])],"derivedFrom":makeQuery(id+"F1MoAnU7Y2teXVl_2.6.F5.boolean.opBoolean","SPLIT",FACE,{"disambiguationData":[TD([subQ3])],"derivedFrom":makeQuery(id+"F1MoAnU7Y2teXVl_2.5.F5.boolean.opBoolean","SPLIT",FACE,{"disambiguationData":[TD([subQ3])],"derivedFrom":makeQuery(id+"F1MoAnU7Y2teXVl_2.4.F5.boolean.opBoolean","SPLIT",FACE,{"disambiguationData":[TD([subQ3])],"derivedFrom":makeQuery(id+"F1MoAnU7Y2teXVl_2.3.F5.boolean.opBoolean","SPLIT",FACE,{"disambiguationData":[TD([subQ3])],"derivedFrom":makeQuery(id+"F1MoAnU7Y2teXVl_2.2.F5.boolean.opBoolean","SPLIT",FACE,{"disambiguationData":[TD([subQ3])],"derivedFrom":makeQuery(id+"F1MoAnU7Y2teXVl_2.1.F5.boolean.opBoolean","SPLIT",FACE,{"disambiguationData":[TD([subQ3])],"derivedFrom":makeQuery(id+"F4.opRevolve","SWEPT_FACE",FACE,{"disambiguationData":[OSD([sQuery(id+"F0.wireOp",EDGE,"E34")])]})})})})})})})})})})})})}),makeQuery(id+"F1MoAnU7Y2teXVl_2.13.F5.opExtrude","SWEPT_FACE",FACE,{"disambiguationData":[OSD([subQ0])]})]});}
            var Q14;
            {var subQ0=sQuery(id+"F1.wireOp",EDGE,"E80");var subQ4=makeQuery(id+"F5.boolean.opBoolean","COPY",FACE,{"derivedFrom":makeQuery(id+"F5.opExtrude","SWEPT_FACE",FACE,{"disambiguationData":[OSD([subQ0])]})});Q14=makeQuery(id+"F1MoAnU7Y2teXVl_2.14.F5.boolean.opBoolean","INTERSECT",EDGE,{"derivedFrom":[makeQuery(id+"F1MoAnU7Y2teXVl_2.13.F5.boolean.opBoolean","SPLIT",FACE,{"disambiguationData":[TD([subQ4])],"derivedFrom":makeQuery(id+"F1MoAnU7Y2teXVl_2.12.F5.boolean.opBoolean","SPLIT",FACE,{"disambiguationData":[TD([subQ4])],"derivedFrom":makeQuery(id+"F1MoAnU7Y2teXVl_2.11.F5.boolean.opBoolean","SPLIT",FACE,{"disambiguationData":[TD([subQ4])],"derivedFrom":makeQuery(id+"F1MoAnU7Y2teXVl_2.10.F5.boolean.opBoolean","SPLIT",FACE,{"disambiguationData":[TD([subQ4])],"derivedFrom":makeQuery(id+"F1MoAnU7Y2teXVl_2.9.F5.boolean.opBoolean","SPLIT",FACE,{"disambiguationData":[TD([subQ4])],"derivedFrom":makeQuery(id+"F1MoAnU7Y2teXVl_2.8.F5.boolean.opBoolean","SPLIT",FACE,{"disambiguationData":[TD([subQ4])],"derivedFrom":makeQuery(id+"F1MoAnU7Y2teXVl_2.7.F5.boolean.opBoolean","SPLIT",FACE,{"disambiguationData":[TD([subQ4])],"derivedFrom":makeQuery(id+"F1MoAnU7Y2teXVl_2.6.F5.boolean.opBoolean","SPLIT",FACE,{"disambiguationData":[TD([subQ4])],"derivedFrom":makeQuery(id+"F1MoAnU7Y2teXVl_2.5.F5.boolean.opBoolean","SPLIT",FACE,{"disambiguationData":[TD([subQ4])],"derivedFrom":makeQuery(id+"F1MoAnU7Y2teXVl_2.4.F5.boolean.opBoolean","SPLIT",FACE,{"disambiguationData":[TD([subQ4])],"derivedFrom":makeQuery(id+"F1MoAnU7Y2teXVl_2.3.F5.boolean.opBoolean","SPLIT",FACE,{"disambiguationData":[TD([subQ4])],"derivedFrom":makeQuery(id+"F1MoAnU7Y2teXVl_2.2.F5.boolean.opBoolean","SPLIT",FACE,{"disambiguationData":[TD([subQ4])],"derivedFrom":makeQuery(id+"F1MoAnU7Y2teXVl_2.1.F5.boolean.opBoolean","SPLIT",FACE,{"disambiguationData":[TD([subQ4])],"derivedFrom":makeQuery(id+"F4.opRevolve","SWEPT_FACE",FACE,{"disambiguationData":[OSD([sQuery(id+"F0.wireOp",EDGE,"E34")])]})})})})})})})})})})})})})}),makeQuery(id+"F1MoAnU7Y2teXVl_2.14.F5.opExtrude","SWEPT_FACE",FACE,{"disambiguationData":[OSD([subQ0])]})]});}
            var Q15;
            {var subQ0=sQuery(id+"F1.wireOp",EDGE,"E80");var subQ3=makeQuery(id+"F5.boolean.opBoolean","COPY",FACE,{"derivedFrom":makeQuery(id+"F5.opExtrude","SWEPT_FACE",FACE,{"disambiguationData":[OSD([subQ0])]})});Q15=makeQuery(id+"F1MoAnU7Y2teXVl_2.15.F5.boolean.opBoolean","INTERSECT",EDGE,{"derivedFrom":[makeQuery(id+"F1MoAnU7Y2teXVl_2.14.F5.boolean.opBoolean","SPLIT",FACE,{"disambiguationData":[TD([subQ3])],"derivedFrom":makeQuery(id+"F1MoAnU7Y2teXVl_2.13.F5.boolean.opBoolean","SPLIT",FACE,{"disambiguationData":[TD([subQ3])],"derivedFrom":makeQuery(id+"F1MoAnU7Y2teXVl_2.12.F5.boolean.opBoolean","SPLIT",FACE,{"disambiguationData":[TD([subQ3])],"derivedFrom":makeQuery(id+"F1MoAnU7Y2teXVl_2.11.F5.boolean.opBoolean","SPLIT",FACE,{"disambiguationData":[TD([subQ3])],"derivedFrom":makeQuery(id+"F1MoAnU7Y2teXVl_2.10.F5.boolean.opBoolean","SPLIT",FACE,{"disambiguationData":[TD([subQ3])],"derivedFrom":makeQuery(id+"F1MoAnU7Y2teXVl_2.9.F5.boolean.opBoolean","SPLIT",FACE,{"disambiguationData":[TD([subQ3])],"derivedFrom":makeQuery(id+"F1MoAnU7Y2teXVl_2.8.F5.boolean.opBoolean","SPLIT",FACE,{"disambiguationData":[TD([subQ3])],"derivedFrom":makeQuery(id+"F1MoAnU7Y2teXVl_2.7.F5.boolean.opBoolean","SPLIT",FACE,{"disambiguationData":[TD([subQ3])],"derivedFrom":makeQuery(id+"F1MoAnU7Y2teXVl_2.6.F5.boolean.opBoolean","SPLIT",FACE,{"disambiguationData":[TD([subQ3])],"derivedFrom":makeQuery(id+"F1MoAnU7Y2teXVl_2.5.F5.boolean.opBoolean","SPLIT",FACE,{"disambiguationData":[TD([subQ3])],"derivedFrom":makeQuery(id+"F1MoAnU7Y2teXVl_2.4.F5.boolean.opBoolean","SPLIT",FACE,{"disambiguationData":[TD([subQ3])],"derivedFrom":makeQuery(id+"F1MoAnU7Y2teXVl_2.3.F5.boolean.opBoolean","SPLIT",FACE,{"disambiguationData":[TD([subQ3])],"derivedFrom":makeQuery(id+"F1MoAnU7Y2teXVl_2.2.F5.boolean.opBoolean","SPLIT",FACE,{"disambiguationData":[TD([subQ3])],"derivedFrom":makeQuery(id+"F1MoAnU7Y2teXVl_2.1.F5.boolean.opBoolean","SPLIT",FACE,{"disambiguationData":[TD([subQ3])],"derivedFrom":makeQuery(id+"F4.opRevolve","SWEPT_FACE",FACE,{"disambiguationData":[OSD([sQuery(id+"F0.wireOp",EDGE,"E34")])]})})})})})})})})})})})})})})}),makeQuery(id+"F1MoAnU7Y2teXVl_2.15.F5.opExtrude","SWEPT_FACE",FACE,{"disambiguationData":[OSD([subQ0])]})]});}
            var Q16;
            {var subQ0=sQuery(id+"F1.wireOp",EDGE,"E79");Q16=makeQuery(id+"F1MoAnU7Y2teXVl_2.2.F5.boolean.opBoolean","INTERSECT",EDGE,{"derivedFrom":[makeQuery(id+"F1MoAnU7Y2teXVl_2.1.F5.boolean.opBoolean","SPLIT",FACE,{"disambiguationData":[TD([makeQuery(id+"F5.boolean.opBoolean","COPY",FACE,{"derivedFrom":makeQuery(id+"F5.opExtrude","SWEPT_FACE",FACE,{"disambiguationData":[OSD([sQuery(id+"F1.wireOp",EDGE,"E80")])]})})])],"derivedFrom":makeQuery(id+"F4.opRevolve","SWEPT_FACE",FACE,{"disambiguationData":[OSD([sQuery(id+"F0.wireOp",EDGE,"E30")])]})}),makeQuery(id+"F1MoAnU7Y2teXVl_2.2.F5.opExtrude","SWEPT_FACE",FACE,{"disambiguationData":[OSD([subQ0])]})]});}
            var Q17;
            Q17=makeQuery(id+"F1MoAnU7Y2teXVl_2.1.F5.boolean.opBoolean","INTERSECT",EDGE,{"derivedFrom":[makeQuery(id+"F4.opRevolve","SWEPT_FACE",FACE,{"disambiguationData":[OSD([sQuery(id+"F0.wireOp",EDGE,"E30")])]}),makeQuery(id+"F1MoAnU7Y2teXVl_2.1.F5.opExtrude","SWEPT_FACE",FACE,{"disambiguationData":[OSD([sQuery(id+"F1.wireOp",EDGE,"E79")])]})]});
            var Q18;
            Q18=makeQuery(id+"F5.boolean.opBoolean","INTERSECT",EDGE,{"derivedFrom":[makeQuery(id+"F4.opRevolve","SWEPT_FACE",FACE,{"disambiguationData":[OSD([sQuery(id+"F0.wireOp",EDGE,"E30")])]}),makeQuery(id+"F5.opExtrude","SWEPT_FACE",FACE,{"disambiguationData":[OSD([sQuery(id+"F1.wireOp",EDGE,"E79")])]})]});
            var Q19;
            {var subQ0=sQuery(id+"F1.wireOp",EDGE,"E79");var subQ3=makeQuery(id+"F5.boolean.opBoolean","COPY",FACE,{"derivedFrom":makeQuery(id+"F5.opExtrude","SWEPT_FACE",FACE,{"disambiguationData":[OSD([sQuery(id+"F1.wireOp",EDGE,"E80")])]})});Q19=makeQuery(id+"F1MoAnU7Y2teXVl_2.15.F5.boolean.opBoolean","INTERSECT",EDGE,{"derivedFrom":[makeQuery(id+"F1MoAnU7Y2teXVl_2.14.F5.boolean.opBoolean","SPLIT",FACE,{"disambiguationData":[TD([subQ3])],"derivedFrom":makeQuery(id+"F1MoAnU7Y2teXVl_2.13.F5.boolean.opBoolean","SPLIT",FACE,{"disambiguationData":[TD([subQ3])],"derivedFrom":makeQuery(id+"F1MoAnU7Y2teXVl_2.12.F5.boolean.opBoolean","SPLIT",FACE,{"disambiguationData":[TD([subQ3])],"derivedFrom":makeQuery(id+"F1MoAnU7Y2teXVl_2.11.F5.boolean.opBoolean","SPLIT",FACE,{"disambiguationData":[TD([subQ3])],"derivedFrom":makeQuery(id+"F1MoAnU7Y2teXVl_2.10.F5.boolean.opBoolean","SPLIT",FACE,{"disambiguationData":[TD([subQ3])],"derivedFrom":makeQuery(id+"F1MoAnU7Y2teXVl_2.9.F5.boolean.opBoolean","SPLIT",FACE,{"disambiguationData":[TD([subQ3])],"derivedFrom":makeQuery(id+"F1MoAnU7Y2teXVl_2.8.F5.boolean.opBoolean","SPLIT",FACE,{"disambiguationData":[TD([subQ3])],"derivedFrom":makeQuery(id+"F1MoAnU7Y2teXVl_2.7.F5.boolean.opBoolean","SPLIT",FACE,{"disambiguationData":[TD([subQ3])],"derivedFrom":makeQuery(id+"F1MoAnU7Y2teXVl_2.6.F5.boolean.opBoolean","SPLIT",FACE,{"disambiguationData":[TD([subQ3])],"derivedFrom":makeQuery(id+"F1MoAnU7Y2teXVl_2.5.F5.boolean.opBoolean","SPLIT",FACE,{"disambiguationData":[TD([subQ3])],"derivedFrom":makeQuery(id+"F1MoAnU7Y2teXVl_2.4.F5.boolean.opBoolean","SPLIT",FACE,{"disambiguationData":[TD([subQ3])],"derivedFrom":makeQuery(id+"F1MoAnU7Y2teXVl_2.3.F5.boolean.opBoolean","SPLIT",FACE,{"disambiguationData":[TD([subQ3])],"derivedFrom":makeQuery(id+"F1MoAnU7Y2teXVl_2.2.F5.boolean.opBoolean","SPLIT",FACE,{"disambiguationData":[TD([subQ3])],"derivedFrom":makeQuery(id+"F1MoAnU7Y2teXVl_2.1.F5.boolean.opBoolean","SPLIT",FACE,{"disambiguationData":[TD([subQ3])],"derivedFrom":makeQuery(id+"F4.opRevolve","SWEPT_FACE",FACE,{"disambiguationData":[OSD([sQuery(id+"F0.wireOp",EDGE,"E30")])]})})})})})})})})})})})})})})}),makeQuery(id+"F1MoAnU7Y2teXVl_2.15.F5.opExtrude","SWEPT_FACE",FACE,{"disambiguationData":[OSD([subQ0])]})]});}
            var Q20;
            {var subQ0=sQuery(id+"F1.wireOp",EDGE,"E79");var subQ3=makeQuery(id+"F5.boolean.opBoolean","COPY",FACE,{"derivedFrom":makeQuery(id+"F5.opExtrude","SWEPT_FACE",FACE,{"disambiguationData":[OSD([sQuery(id+"F1.wireOp",EDGE,"E80")])]})});Q20=makeQuery(id+"F1MoAnU7Y2teXVl_2.14.F5.boolean.opBoolean","INTERSECT",EDGE,{"derivedFrom":[makeQuery(id+"F1MoAnU7Y2teXVl_2.13.F5.boolean.opBoolean","SPLIT",FACE,{"disambiguationData":[TD([subQ3])],"derivedFrom":makeQuery(id+"F1MoAnU7Y2teXVl_2.12.F5.boolean.opBoolean","SPLIT",FACE,{"disambiguationData":[TD([subQ3])],"derivedFrom":makeQuery(id+"F1MoAnU7Y2teXVl_2.11.F5.boolean.opBoolean","SPLIT",FACE,{"disambiguationData":[TD([subQ3])],"derivedFrom":makeQuery(id+"F1MoAnU7Y2teXVl_2.10.F5.boolean.opBoolean","SPLIT",FACE,{"disambiguationData":[TD([subQ3])],"derivedFrom":makeQuery(id+"F1MoAnU7Y2teXVl_2.9.F5.boolean.opBoolean","SPLIT",FACE,{"disambiguationData":[TD([subQ3])],"derivedFrom":makeQuery(id+"F1MoAnU7Y2teXVl_2.8.F5.boolean.opBoolean","SPLIT",FACE,{"disambiguationData":[TD([subQ3])],"derivedFrom":makeQuery(id+"F1MoAnU7Y2teXVl_2.7.F5.boolean.opBoolean","SPLIT",FACE,{"disambiguationData":[TD([subQ3])],"derivedFrom":makeQuery(id+"F1MoAnU7Y2teXVl_2.6.F5.boolean.opBoolean","SPLIT",FACE,{"disambiguationData":[TD([subQ3])],"derivedFrom":makeQuery(id+"F1MoAnU7Y2teXVl_2.5.F5.boolean.opBoolean","SPLIT",FACE,{"disambiguationData":[TD([subQ3])],"derivedFrom":makeQuery(id+"F1MoAnU7Y2teXVl_2.4.F5.boolean.opBoolean","SPLIT",FACE,{"disambiguationData":[TD([subQ3])],"derivedFrom":makeQuery(id+"F1MoAnU7Y2teXVl_2.3.F5.boolean.opBoolean","SPLIT",FACE,{"disambiguationData":[TD([subQ3])],"derivedFrom":makeQuery(id+"F1MoAnU7Y2teXVl_2.2.F5.boolean.opBoolean","SPLIT",FACE,{"disambiguationData":[TD([subQ3])],"derivedFrom":makeQuery(id+"F1MoAnU7Y2teXVl_2.1.F5.boolean.opBoolean","SPLIT",FACE,{"disambiguationData":[TD([subQ3])],"derivedFrom":makeQuery(id+"F4.opRevolve","SWEPT_FACE",FACE,{"disambiguationData":[OSD([sQuery(id+"F0.wireOp",EDGE,"E30")])]})})})})})})})})})})})})})}),makeQuery(id+"F1MoAnU7Y2teXVl_2.14.F5.opExtrude","SWEPT_FACE",FACE,{"disambiguationData":[OSD([subQ0])]})]});}
            var Q21;
            {var subQ0=sQuery(id+"F1.wireOp",EDGE,"E79");var subQ3=makeQuery(id+"F5.boolean.opBoolean","COPY",FACE,{"derivedFrom":makeQuery(id+"F5.opExtrude","SWEPT_FACE",FACE,{"disambiguationData":[OSD([sQuery(id+"F1.wireOp",EDGE,"E80")])]})});Q21=makeQuery(id+"F1MoAnU7Y2teXVl_2.13.F5.boolean.opBoolean","INTERSECT",EDGE,{"derivedFrom":[makeQuery(id+"F1MoAnU7Y2teXVl_2.12.F5.boolean.opBoolean","SPLIT",FACE,{"disambiguationData":[TD([subQ3])],"derivedFrom":makeQuery(id+"F1MoAnU7Y2teXVl_2.11.F5.boolean.opBoolean","SPLIT",FACE,{"disambiguationData":[TD([subQ3])],"derivedFrom":makeQuery(id+"F1MoAnU7Y2teXVl_2.10.F5.boolean.opBoolean","SPLIT",FACE,{"disambiguationData":[TD([subQ3])],"derivedFrom":makeQuery(id+"F1MoAnU7Y2teXVl_2.9.F5.boolean.opBoolean","SPLIT",FACE,{"disambiguationData":[TD([subQ3])],"derivedFrom":makeQuery(id+"F1MoAnU7Y2teXVl_2.8.F5.boolean.opBoolean","SPLIT",FACE,{"disambiguationData":[TD([subQ3])],"derivedFrom":makeQuery(id+"F1MoAnU7Y2teXVl_2.7.F5.boolean.opBoolean","SPLIT",FACE,{"disambiguationData":[TD([subQ3])],"derivedFrom":makeQuery(id+"F1MoAnU7Y2teXVl_2.6.F5.boolean.opBoolean","SPLIT",FACE,{"disambiguationData":[TD([subQ3])],"derivedFrom":makeQuery(id+"F1MoAnU7Y2teXVl_2.5.F5.boolean.opBoolean","SPLIT",FACE,{"disambiguationData":[TD([subQ3])],"derivedFrom":makeQuery(id+"F1MoAnU7Y2teXVl_2.4.F5.boolean.opBoolean","SPLIT",FACE,{"disambiguationData":[TD([subQ3])],"derivedFrom":makeQuery(id+"F1MoAnU7Y2teXVl_2.3.F5.boolean.opBoolean","SPLIT",FACE,{"disambiguationData":[TD([subQ3])],"derivedFrom":makeQuery(id+"F1MoAnU7Y2teXVl_2.2.F5.boolean.opBoolean","SPLIT",FACE,{"disambiguationData":[TD([subQ3])],"derivedFrom":makeQuery(id+"F1MoAnU7Y2teXVl_2.1.F5.boolean.opBoolean","SPLIT",FACE,{"disambiguationData":[TD([subQ3])],"derivedFrom":makeQuery(id+"F4.opRevolve","SWEPT_FACE",FACE,{"disambiguationData":[OSD([sQuery(id+"F0.wireOp",EDGE,"E30")])]})})})})})})})})})})})})}),makeQuery(id+"F1MoAnU7Y2teXVl_2.13.F5.opExtrude","SWEPT_FACE",FACE,{"disambiguationData":[OSD([subQ0])]})]});}
            var Q22;
            {var subQ0=sQuery(id+"F1.wireOp",EDGE,"E79");var subQ3=makeQuery(id+"F5.boolean.opBoolean","COPY",FACE,{"derivedFrom":makeQuery(id+"F5.opExtrude","SWEPT_FACE",FACE,{"disambiguationData":[OSD([sQuery(id+"F1.wireOp",EDGE,"E80")])]})});Q22=makeQuery(id+"F1MoAnU7Y2teXVl_2.12.F5.boolean.opBoolean","INTERSECT",EDGE,{"derivedFrom":[makeQuery(id+"F1MoAnU7Y2teXVl_2.11.F5.boolean.opBoolean","SPLIT",FACE,{"disambiguationData":[TD([subQ3])],"derivedFrom":makeQuery(id+"F1MoAnU7Y2teXVl_2.10.F5.boolean.opBoolean","SPLIT",FACE,{"disambiguationData":[TD([subQ3])],"derivedFrom":makeQuery(id+"F1MoAnU7Y2teXVl_2.9.F5.boolean.opBoolean","SPLIT",FACE,{"disambiguationData":[TD([subQ3])],"derivedFrom":makeQuery(id+"F1MoAnU7Y2teXVl_2.8.F5.boolean.opBoolean","SPLIT",FACE,{"disambiguationData":[TD([subQ3])],"derivedFrom":makeQuery(id+"F1MoAnU7Y2teXVl_2.7.F5.boolean.opBoolean","SPLIT",FACE,{"disambiguationData":[TD([subQ3])],"derivedFrom":makeQuery(id+"F1MoAnU7Y2teXVl_2.6.F5.boolean.opBoolean","SPLIT",FACE,{"disambiguationData":[TD([subQ3])],"derivedFrom":makeQuery(id+"F1MoAnU7Y2teXVl_2.5.F5.boolean.opBoolean","SPLIT",FACE,{"disambiguationData":[TD([subQ3])],"derivedFrom":makeQuery(id+"F1MoAnU7Y2teXVl_2.4.F5.boolean.opBoolean","SPLIT",FACE,{"disambiguationData":[TD([subQ3])],"derivedFrom":makeQuery(id+"F1MoAnU7Y2teXVl_2.3.F5.boolean.opBoolean","SPLIT",FACE,{"disambiguationData":[TD([subQ3])],"derivedFrom":makeQuery(id+"F1MoAnU7Y2teXVl_2.2.F5.boolean.opBoolean","SPLIT",FACE,{"disambiguationData":[TD([subQ3])],"derivedFrom":makeQuery(id+"F1MoAnU7Y2teXVl_2.1.F5.boolean.opBoolean","SPLIT",FACE,{"disambiguationData":[TD([subQ3])],"derivedFrom":makeQuery(id+"F4.opRevolve","SWEPT_FACE",FACE,{"disambiguationData":[OSD([sQuery(id+"F0.wireOp",EDGE,"E30")])]})})})})})})})})})})})}),makeQuery(id+"F1MoAnU7Y2teXVl_2.12.F5.opExtrude","SWEPT_FACE",FACE,{"disambiguationData":[OSD([subQ0])]})]});}
            var Q23;
            {var subQ0=sQuery(id+"F1.wireOp",EDGE,"E79");var subQ3=makeQuery(id+"F5.boolean.opBoolean","COPY",FACE,{"derivedFrom":makeQuery(id+"F5.opExtrude","SWEPT_FACE",FACE,{"disambiguationData":[OSD([sQuery(id+"F1.wireOp",EDGE,"E80")])]})});Q23=makeQuery(id+"F1MoAnU7Y2teXVl_2.11.F5.boolean.opBoolean","INTERSECT",EDGE,{"derivedFrom":[makeQuery(id+"F1MoAnU7Y2teXVl_2.10.F5.boolean.opBoolean","SPLIT",FACE,{"disambiguationData":[TD([subQ3])],"derivedFrom":makeQuery(id+"F1MoAnU7Y2teXVl_2.9.F5.boolean.opBoolean","SPLIT",FACE,{"disambiguationData":[TD([subQ3])],"derivedFrom":makeQuery(id+"F1MoAnU7Y2teXVl_2.8.F5.boolean.opBoolean","SPLIT",FACE,{"disambiguationData":[TD([subQ3])],"derivedFrom":makeQuery(id+"F1MoAnU7Y2teXVl_2.7.F5.boolean.opBoolean","SPLIT",FACE,{"disambiguationData":[TD([subQ3])],"derivedFrom":makeQuery(id+"F1MoAnU7Y2teXVl_2.6.F5.boolean.opBoolean","SPLIT",FACE,{"disambiguationData":[TD([subQ3])],"derivedFrom":makeQuery(id+"F1MoAnU7Y2teXVl_2.5.F5.boolean.opBoolean","SPLIT",FACE,{"disambiguationData":[TD([subQ3])],"derivedFrom":makeQuery(id+"F1MoAnU7Y2teXVl_2.4.F5.boolean.opBoolean","SPLIT",FACE,{"disambiguationData":[TD([subQ3])],"derivedFrom":makeQuery(id+"F1MoAnU7Y2teXVl_2.3.F5.boolean.opBoolean","SPLIT",FACE,{"disambiguationData":[TD([subQ3])],"derivedFrom":makeQuery(id+"F1MoAnU7Y2teXVl_2.2.F5.boolean.opBoolean","SPLIT",FACE,{"disambiguationData":[TD([subQ3])],"derivedFrom":makeQuery(id+"F1MoAnU7Y2teXVl_2.1.F5.boolean.opBoolean","SPLIT",FACE,{"disambiguationData":[TD([subQ3])],"derivedFrom":makeQuery(id+"F4.opRevolve","SWEPT_FACE",FACE,{"disambiguationData":[OSD([sQuery(id+"F0.wireOp",EDGE,"E30")])]})})})})})})})})})})}),makeQuery(id+"F1MoAnU7Y2teXVl_2.11.F5.opExtrude","SWEPT_FACE",FACE,{"disambiguationData":[OSD([subQ0])]})]});}
            var Q24;
            {var subQ0=sQuery(id+"F1.wireOp",EDGE,"E79");var subQ3=makeQuery(id+"F5.boolean.opBoolean","COPY",FACE,{"derivedFrom":makeQuery(id+"F5.opExtrude","SWEPT_FACE",FACE,{"disambiguationData":[OSD([sQuery(id+"F1.wireOp",EDGE,"E80")])]})});Q24=makeQuery(id+"F1MoAnU7Y2teXVl_2.10.F5.boolean.opBoolean","INTERSECT",EDGE,{"derivedFrom":[makeQuery(id+"F1MoAnU7Y2teXVl_2.9.F5.boolean.opBoolean","SPLIT",FACE,{"disambiguationData":[TD([subQ3])],"derivedFrom":makeQuery(id+"F1MoAnU7Y2teXVl_2.8.F5.boolean.opBoolean","SPLIT",FACE,{"disambiguationData":[TD([subQ3])],"derivedFrom":makeQuery(id+"F1MoAnU7Y2teXVl_2.7.F5.boolean.opBoolean","SPLIT",FACE,{"disambiguationData":[TD([subQ3])],"derivedFrom":makeQuery(id+"F1MoAnU7Y2teXVl_2.6.F5.boolean.opBoolean","SPLIT",FACE,{"disambiguationData":[TD([subQ3])],"derivedFrom":makeQuery(id+"F1MoAnU7Y2teXVl_2.5.F5.boolean.opBoolean","SPLIT",FACE,{"disambiguationData":[TD([subQ3])],"derivedFrom":makeQuery(id+"F1MoAnU7Y2teXVl_2.4.F5.boolean.opBoolean","SPLIT",FACE,{"disambiguationData":[TD([subQ3])],"derivedFrom":makeQuery(id+"F1MoAnU7Y2teXVl_2.3.F5.boolean.opBoolean","SPLIT",FACE,{"disambiguationData":[TD([subQ3])],"derivedFrom":makeQuery(id+"F1MoAnU7Y2teXVl_2.2.F5.boolean.opBoolean","SPLIT",FACE,{"disambiguationData":[TD([subQ3])],"derivedFrom":makeQuery(id+"F1MoAnU7Y2teXVl_2.1.F5.boolean.opBoolean","SPLIT",FACE,{"disambiguationData":[TD([subQ3])],"derivedFrom":makeQuery(id+"F4.opRevolve","SWEPT_FACE",FACE,{"disambiguationData":[OSD([sQuery(id+"F0.wireOp",EDGE,"E30")])]})})})})})})})})})}),makeQuery(id+"F1MoAnU7Y2teXVl_2.10.F5.opExtrude","SWEPT_FACE",FACE,{"disambiguationData":[OSD([subQ0])]})]});}
            var Q25;
            {var subQ0=sQuery(id+"F1.wireOp",EDGE,"E79");var subQ3=makeQuery(id+"F5.boolean.opBoolean","COPY",FACE,{"derivedFrom":makeQuery(id+"F5.opExtrude","SWEPT_FACE",FACE,{"disambiguationData":[OSD([sQuery(id+"F1.wireOp",EDGE,"E80")])]})});Q25=makeQuery(id+"F1MoAnU7Y2teXVl_2.9.F5.boolean.opBoolean","INTERSECT",EDGE,{"derivedFrom":[makeQuery(id+"F1MoAnU7Y2teXVl_2.8.F5.boolean.opBoolean","SPLIT",FACE,{"disambiguationData":[TD([subQ3])],"derivedFrom":makeQuery(id+"F1MoAnU7Y2teXVl_2.7.F5.boolean.opBoolean","SPLIT",FACE,{"disambiguationData":[TD([subQ3])],"derivedFrom":makeQuery(id+"F1MoAnU7Y2teXVl_2.6.F5.boolean.opBoolean","SPLIT",FACE,{"disambiguationData":[TD([subQ3])],"derivedFrom":makeQuery(id+"F1MoAnU7Y2teXVl_2.5.F5.boolean.opBoolean","SPLIT",FACE,{"disambiguationData":[TD([subQ3])],"derivedFrom":makeQuery(id+"F1MoAnU7Y2teXVl_2.4.F5.boolean.opBoolean","SPLIT",FACE,{"disambiguationData":[TD([subQ3])],"derivedFrom":makeQuery(id+"F1MoAnU7Y2teXVl_2.3.F5.boolean.opBoolean","SPLIT",FACE,{"disambiguationData":[TD([subQ3])],"derivedFrom":makeQuery(id+"F1MoAnU7Y2teXVl_2.2.F5.boolean.opBoolean","SPLIT",FACE,{"disambiguationData":[TD([subQ3])],"derivedFrom":makeQuery(id+"F1MoAnU7Y2teXVl_2.1.F5.boolean.opBoolean","SPLIT",FACE,{"disambiguationData":[TD([subQ3])],"derivedFrom":makeQuery(id+"F4.opRevolve","SWEPT_FACE",FACE,{"disambiguationData":[OSD([sQuery(id+"F0.wireOp",EDGE,"E30")])]})})})})})})})})}),makeQuery(id+"F1MoAnU7Y2teXVl_2.9.F5.opExtrude","SWEPT_FACE",FACE,{"disambiguationData":[OSD([subQ0])]})]});}
            var Q26;
            {var subQ0=sQuery(id+"F1.wireOp",EDGE,"E79");var subQ3=makeQuery(id+"F5.boolean.opBoolean","COPY",FACE,{"derivedFrom":makeQuery(id+"F5.opExtrude","SWEPT_FACE",FACE,{"disambiguationData":[OSD([sQuery(id+"F1.wireOp",EDGE,"E80")])]})});Q26=makeQuery(id+"F1MoAnU7Y2teXVl_2.8.F5.boolean.opBoolean","INTERSECT",EDGE,{"derivedFrom":[makeQuery(id+"F1MoAnU7Y2teXVl_2.7.F5.boolean.opBoolean","SPLIT",FACE,{"disambiguationData":[TD([subQ3])],"derivedFrom":makeQuery(id+"F1MoAnU7Y2teXVl_2.6.F5.boolean.opBoolean","SPLIT",FACE,{"disambiguationData":[TD([subQ3])],"derivedFrom":makeQuery(id+"F1MoAnU7Y2teXVl_2.5.F5.boolean.opBoolean","SPLIT",FACE,{"disambiguationData":[TD([subQ3])],"derivedFrom":makeQuery(id+"F1MoAnU7Y2teXVl_2.4.F5.boolean.opBoolean","SPLIT",FACE,{"disambiguationData":[TD([subQ3])],"derivedFrom":makeQuery(id+"F1MoAnU7Y2teXVl_2.3.F5.boolean.opBoolean","SPLIT",FACE,{"disambiguationData":[TD([subQ3])],"derivedFrom":makeQuery(id+"F1MoAnU7Y2teXVl_2.2.F5.boolean.opBoolean","SPLIT",FACE,{"disambiguationData":[TD([subQ3])],"derivedFrom":makeQuery(id+"F1MoAnU7Y2teXVl_2.1.F5.boolean.opBoolean","SPLIT",FACE,{"disambiguationData":[TD([subQ3])],"derivedFrom":makeQuery(id+"F4.opRevolve","SWEPT_FACE",FACE,{"disambiguationData":[OSD([sQuery(id+"F0.wireOp",EDGE,"E30")])]})})})})})})})}),makeQuery(id+"F1MoAnU7Y2teXVl_2.8.F5.opExtrude","SWEPT_FACE",FACE,{"disambiguationData":[OSD([subQ0])]})]});}
            var Q27;
            {var subQ0=sQuery(id+"F1.wireOp",EDGE,"E79");var subQ3=makeQuery(id+"F5.boolean.opBoolean","COPY",FACE,{"derivedFrom":makeQuery(id+"F5.opExtrude","SWEPT_FACE",FACE,{"disambiguationData":[OSD([sQuery(id+"F1.wireOp",EDGE,"E80")])]})});Q27=makeQuery(id+"F1MoAnU7Y2teXVl_2.7.F5.boolean.opBoolean","INTERSECT",EDGE,{"derivedFrom":[makeQuery(id+"F1MoAnU7Y2teXVl_2.6.F5.boolean.opBoolean","SPLIT",FACE,{"disambiguationData":[TD([subQ3])],"derivedFrom":makeQuery(id+"F1MoAnU7Y2teXVl_2.5.F5.boolean.opBoolean","SPLIT",FACE,{"disambiguationData":[TD([subQ3])],"derivedFrom":makeQuery(id+"F1MoAnU7Y2teXVl_2.4.F5.boolean.opBoolean","SPLIT",FACE,{"disambiguationData":[TD([subQ3])],"derivedFrom":makeQuery(id+"F1MoAnU7Y2teXVl_2.3.F5.boolean.opBoolean","SPLIT",FACE,{"disambiguationData":[TD([subQ3])],"derivedFrom":makeQuery(id+"F1MoAnU7Y2teXVl_2.2.F5.boolean.opBoolean","SPLIT",FACE,{"disambiguationData":[TD([subQ3])],"derivedFrom":makeQuery(id+"F1MoAnU7Y2teXVl_2.1.F5.boolean.opBoolean","SPLIT",FACE,{"disambiguationData":[TD([subQ3])],"derivedFrom":makeQuery(id+"F4.opRevolve","SWEPT_FACE",FACE,{"disambiguationData":[OSD([sQuery(id+"F0.wireOp",EDGE,"E30")])]})})})})})})}),makeQuery(id+"F1MoAnU7Y2teXVl_2.7.F5.opExtrude","SWEPT_FACE",FACE,{"disambiguationData":[OSD([subQ0])]})]});}
            var Q28;
            {var subQ0=sQuery(id+"F1.wireOp",EDGE,"E79");var subQ3=makeQuery(id+"F5.boolean.opBoolean","COPY",FACE,{"derivedFrom":makeQuery(id+"F5.opExtrude","SWEPT_FACE",FACE,{"disambiguationData":[OSD([sQuery(id+"F1.wireOp",EDGE,"E80")])]})});Q28=makeQuery(id+"F1MoAnU7Y2teXVl_2.6.F5.boolean.opBoolean","INTERSECT",EDGE,{"derivedFrom":[makeQuery(id+"F1MoAnU7Y2teXVl_2.5.F5.boolean.opBoolean","SPLIT",FACE,{"disambiguationData":[TD([subQ3])],"derivedFrom":makeQuery(id+"F1MoAnU7Y2teXVl_2.4.F5.boolean.opBoolean","SPLIT",FACE,{"disambiguationData":[TD([subQ3])],"derivedFrom":makeQuery(id+"F1MoAnU7Y2teXVl_2.3.F5.boolean.opBoolean","SPLIT",FACE,{"disambiguationData":[TD([subQ3])],"derivedFrom":makeQuery(id+"F1MoAnU7Y2teXVl_2.2.F5.boolean.opBoolean","SPLIT",FACE,{"disambiguationData":[TD([subQ3])],"derivedFrom":makeQuery(id+"F1MoAnU7Y2teXVl_2.1.F5.boolean.opBoolean","SPLIT",FACE,{"disambiguationData":[TD([subQ3])],"derivedFrom":makeQuery(id+"F4.opRevolve","SWEPT_FACE",FACE,{"disambiguationData":[OSD([sQuery(id+"F0.wireOp",EDGE,"E30")])]})})})})})}),makeQuery(id+"F1MoAnU7Y2teXVl_2.6.F5.opExtrude","SWEPT_FACE",FACE,{"disambiguationData":[OSD([subQ0])]})]});}
            var Q29;
            {var subQ0=sQuery(id+"F1.wireOp",EDGE,"E79");var subQ3=makeQuery(id+"F5.boolean.opBoolean","COPY",FACE,{"derivedFrom":makeQuery(id+"F5.opExtrude","SWEPT_FACE",FACE,{"disambiguationData":[OSD([sQuery(id+"F1.wireOp",EDGE,"E80")])]})});Q29=makeQuery(id+"F1MoAnU7Y2teXVl_2.5.F5.boolean.opBoolean","INTERSECT",EDGE,{"derivedFrom":[makeQuery(id+"F1MoAnU7Y2teXVl_2.4.F5.boolean.opBoolean","SPLIT",FACE,{"disambiguationData":[TD([subQ3])],"derivedFrom":makeQuery(id+"F1MoAnU7Y2teXVl_2.3.F5.boolean.opBoolean","SPLIT",FACE,{"disambiguationData":[TD([subQ3])],"derivedFrom":makeQuery(id+"F1MoAnU7Y2teXVl_2.2.F5.boolean.opBoolean","SPLIT",FACE,{"disambiguationData":[TD([subQ3])],"derivedFrom":makeQuery(id+"F1MoAnU7Y2teXVl_2.1.F5.boolean.opBoolean","SPLIT",FACE,{"disambiguationData":[TD([subQ3])],"derivedFrom":makeQuery(id+"F4.opRevolve","SWEPT_FACE",FACE,{"disambiguationData":[OSD([sQuery(id+"F0.wireOp",EDGE,"E30")])]})})})})}),makeQuery(id+"F1MoAnU7Y2teXVl_2.5.F5.opExtrude","SWEPT_FACE",FACE,{"disambiguationData":[OSD([subQ0])]})]});}
            var Q30;
            {var subQ0=sQuery(id+"F1.wireOp",EDGE,"E79");var subQ3=makeQuery(id+"F5.boolean.opBoolean","COPY",FACE,{"derivedFrom":makeQuery(id+"F5.opExtrude","SWEPT_FACE",FACE,{"disambiguationData":[OSD([sQuery(id+"F1.wireOp",EDGE,"E80")])]})});Q30=makeQuery(id+"F1MoAnU7Y2teXVl_2.4.F5.boolean.opBoolean","INTERSECT",EDGE,{"derivedFrom":[makeQuery(id+"F1MoAnU7Y2teXVl_2.3.F5.boolean.opBoolean","SPLIT",FACE,{"disambiguationData":[TD([subQ3])],"derivedFrom":makeQuery(id+"F1MoAnU7Y2teXVl_2.2.F5.boolean.opBoolean","SPLIT",FACE,{"disambiguationData":[TD([subQ3])],"derivedFrom":makeQuery(id+"F1MoAnU7Y2teXVl_2.1.F5.boolean.opBoolean","SPLIT",FACE,{"disambiguationData":[TD([subQ3])],"derivedFrom":makeQuery(id+"F4.opRevolve","SWEPT_FACE",FACE,{"disambiguationData":[OSD([sQuery(id+"F0.wireOp",EDGE,"E30")])]})})})}),makeQuery(id+"F1MoAnU7Y2teXVl_2.4.F5.opExtrude","SWEPT_FACE",FACE,{"disambiguationData":[OSD([subQ0])]})]});}
            var Q31;
            {var subQ0=sQuery(id+"F1.wireOp",EDGE,"E79");var subQ3=makeQuery(id+"F5.boolean.opBoolean","COPY",FACE,{"derivedFrom":makeQuery(id+"F5.opExtrude","SWEPT_FACE",FACE,{"disambiguationData":[OSD([sQuery(id+"F1.wireOp",EDGE,"E80")])]})});Q31=makeQuery(id+"F1MoAnU7Y2teXVl_2.3.F5.boolean.opBoolean","INTERSECT",EDGE,{"derivedFrom":[makeQuery(id+"F1MoAnU7Y2teXVl_2.2.F5.boolean.opBoolean","SPLIT",FACE,{"disambiguationData":[TD([subQ3])],"derivedFrom":makeQuery(id+"F1MoAnU7Y2teXVl_2.1.F5.boolean.opBoolean","SPLIT",FACE,{"disambiguationData":[TD([subQ3])],"derivedFrom":makeQuery(id+"F4.opRevolve","SWEPT_FACE",FACE,{"disambiguationData":[OSD([sQuery(id+"F0.wireOp",EDGE,"E30")])]})})}),makeQuery(id+"F1MoAnU7Y2teXVl_2.3.F5.opExtrude","SWEPT_FACE",FACE,{"disambiguationData":[OSD([subQ0])]})]});}
            fillet(context, id + "F6", {"entities" : qUnion([Q0, Q1, Q2, Q3, Q4, Q5, Q6, Q7, Q8, Q9, Q10, Q11, Q12, Q13, Q14, Q15, Q16, Q17, Q18, Q19, Q20, Q21, Q22, Q23, Q24, Q25, Q26, Q27, Q28, Q29, Q30, Q31]), "radius" : 2 * mm, "tangentPropagation" : true, "allowEdgeOverflow" : false});
        }
        {
            var Q0;
            {var subQ0=sQuery(id+"F0.wireOp",EDGE,"E2");var subQ2=sQuery(id+"F1.wireOp",EDGE,"E80");var subQ3=sQuery(id+"F0.wireOp",EDGE,"E29");var subQ5=sQuery(id+"F1.wireOp",EDGE,"E79");var subQ6=makeQuery(id+"F1MoAnU7Y2teXVl_2.8.F5.opExtrude","SWEPT_FACE",FACE,{"disambiguationData":[OSD([subQ5])]});var subQ7=makeQuery(id+"F5.boolean.opBoolean","COPY",FACE,{"derivedFrom":makeQuery(id+"F5.opExtrude","SWEPT_FACE",FACE,{"disambiguationData":[OSD([subQ2])]})});Q0=makeQuery(id+"F1MoAnU7Y2teXVl_2.9.F5.boolean.opBoolean","SPLIT",EDGE,{"disambiguationData":[TD([makeQuery(id+"F1MoAnU7Y2teXVl_2.8.F5.boolean.opBoolean","COPY",FACE,{"derivedFrom":subQ6})])],"derivedFrom":makeQuery(id+"F1MoAnU7Y2teXVl_2.8.F5.boolean.opBoolean","SPLIT",EDGE,{"disambiguationData":[TD([subQ7])],"derivedFrom":makeQuery(id+"F1MoAnU7Y2teXVl_2.7.F5.boolean.opBoolean","SPLIT",EDGE,{"disambiguationData":[TD([subQ7])],"derivedFrom":makeQuery(id+"F1MoAnU7Y2teXVl_2.6.F5.boolean.opBoolean","SPLIT",EDGE,{"disambiguationData":[TD([subQ7])],"derivedFrom":makeQuery(id+"F1MoAnU7Y2teXVl_2.5.F5.boolean.opBoolean","SPLIT",EDGE,{"disambiguationData":[TD([subQ7])],"derivedFrom":makeQuery(id+"F1MoAnU7Y2teXVl_2.4.F5.boolean.opBoolean","SPLIT",EDGE,{"disambiguationData":[TD([subQ7])],"derivedFrom":makeQuery(id+"F1MoAnU7Y2teXVl_2.3.F5.boolean.opBoolean","SPLIT",EDGE,{"disambiguationData":[TD([subQ7])],"derivedFrom":makeQuery(id+"F1MoAnU7Y2teXVl_2.2.F5.boolean.opBoolean","SPLIT",EDGE,{"disambiguationData":[TD([subQ7])],"derivedFrom":makeQuery(id+"F1MoAnU7Y2teXVl_2.1.F5.boolean.opBoolean","SPLIT",EDGE,{"disambiguationData":[TD([subQ7])],"derivedFrom":makeQuery(id+"F4.opRevolve","SWEPT_EDGE",EDGE,{"disambiguationData":[OSD([subQ0,subQ3])]})})})})})})})})})});}
            var Q1;
            {var subQ0=sQuery(id+"F0.wireOp",EDGE,"E2");var subQ2=sQuery(id+"F0.wireOp",EDGE,"E29");var subQ4=makeQuery(id+"F5.boolean.opBoolean","COPY",FACE,{"derivedFrom":makeQuery(id+"F5.opExtrude","SWEPT_FACE",FACE,{"disambiguationData":[OSD([sQuery(id+"F1.wireOp",EDGE,"E80")])]})});Q1=makeQuery(id+"F1MoAnU7Y2teXVl_2.9.F5.boolean.opBoolean","SPLIT",EDGE,{"disambiguationData":[TD([subQ4])],"derivedFrom":makeQuery(id+"F1MoAnU7Y2teXVl_2.8.F5.boolean.opBoolean","SPLIT",EDGE,{"disambiguationData":[TD([subQ4])],"derivedFrom":makeQuery(id+"F1MoAnU7Y2teXVl_2.7.F5.boolean.opBoolean","SPLIT",EDGE,{"disambiguationData":[TD([subQ4])],"derivedFrom":makeQuery(id+"F1MoAnU7Y2teXVl_2.6.F5.boolean.opBoolean","SPLIT",EDGE,{"disambiguationData":[TD([subQ4])],"derivedFrom":makeQuery(id+"F1MoAnU7Y2teXVl_2.5.F5.boolean.opBoolean","SPLIT",EDGE,{"disambiguationData":[TD([subQ4])],"derivedFrom":makeQuery(id+"F1MoAnU7Y2teXVl_2.4.F5.boolean.opBoolean","SPLIT",EDGE,{"disambiguationData":[TD([subQ4])],"derivedFrom":makeQuery(id+"F1MoAnU7Y2teXVl_2.3.F5.boolean.opBoolean","SPLIT",EDGE,{"disambiguationData":[TD([subQ4])],"derivedFrom":makeQuery(id+"F1MoAnU7Y2teXVl_2.2.F5.boolean.opBoolean","SPLIT",EDGE,{"disambiguationData":[TD([subQ4])],"derivedFrom":makeQuery(id+"F1MoAnU7Y2teXVl_2.1.F5.boolean.opBoolean","SPLIT",EDGE,{"disambiguationData":[TD([subQ4])],"derivedFrom":makeQuery(id+"F4.opRevolve","SWEPT_EDGE",EDGE,{"disambiguationData":[OSD([subQ0,subQ2])]})})})})})})})})})});}
            var Q2;
            {var subQ0=sQuery(id+"F0.wireOp",EDGE,"E2");var subQ1=sQuery(id+"F0.wireOp",EDGE,"E29");Q2=makeQuery(id+"F1MoAnU7Y2teXVl_2.1.F5.boolean.opBoolean","SPLIT",EDGE,{"disambiguationData":[TD([makeQuery(id+"F5.boolean.opBoolean","COPY",FACE,{"derivedFrom":makeQuery(id+"F5.opExtrude","SWEPT_FACE",FACE,{"disambiguationData":[OSD([sQuery(id+"F1.wireOp",EDGE,"E79")])]})})])],"derivedFrom":makeQuery(id+"F4.opRevolve","SWEPT_EDGE",EDGE,{"disambiguationData":[OSD([subQ0,subQ1])]})});}
            var Q3;
            {var subQ0=sQuery(id+"F0.wireOp",EDGE,"E2");var subQ2=sQuery(id+"F0.wireOp",EDGE,"E29");var subQ4=makeQuery(id+"F1MoAnU7Y2teXVl_2.1.F5.opExtrude","SWEPT_FACE",FACE,{"disambiguationData":[OSD([sQuery(id+"F1.wireOp",EDGE,"E79")])]});var subQ5=sQuery(id+"F1.wireOp",EDGE,"E80");Q3=makeQuery(id+"F1MoAnU7Y2teXVl_2.2.F5.boolean.opBoolean","SPLIT",EDGE,{"disambiguationData":[TD([makeQuery(id+"F1MoAnU7Y2teXVl_2.1.F5.boolean.opBoolean","COPY",FACE,{"derivedFrom":subQ4})])],"derivedFrom":makeQuery(id+"F1MoAnU7Y2teXVl_2.1.F5.boolean.opBoolean","SPLIT",EDGE,{"disambiguationData":[TD([makeQuery(id+"F5.boolean.opBoolean","COPY",FACE,{"derivedFrom":makeQuery(id+"F5.opExtrude","SWEPT_FACE",FACE,{"disambiguationData":[OSD([subQ5])]})})])],"derivedFrom":makeQuery(id+"F4.opRevolve","SWEPT_EDGE",EDGE,{"disambiguationData":[OSD([subQ0,subQ2])]})})});}
            var Q4;
            {var subQ0=sQuery(id+"F0.wireOp",EDGE,"E2");var subQ2=sQuery(id+"F0.wireOp",EDGE,"E29");var subQ4=sQuery(id+"F1.wireOp",EDGE,"E79");var subQ5=makeQuery(id+"F1MoAnU7Y2teXVl_2.2.F5.opExtrude","SWEPT_FACE",FACE,{"disambiguationData":[OSD([subQ4])]});var subQ6=sQuery(id+"F1.wireOp",EDGE,"E80");var subQ7=makeQuery(id+"F5.boolean.opBoolean","COPY",FACE,{"derivedFrom":makeQuery(id+"F5.opExtrude","SWEPT_FACE",FACE,{"disambiguationData":[OSD([subQ6])]})});Q4=makeQuery(id+"F1MoAnU7Y2teXVl_2.3.F5.boolean.opBoolean","SPLIT",EDGE,{"disambiguationData":[TD([makeQuery(id+"F1MoAnU7Y2teXVl_2.2.F5.boolean.opBoolean","COPY",FACE,{"derivedFrom":subQ5})])],"derivedFrom":makeQuery(id+"F1MoAnU7Y2teXVl_2.2.F5.boolean.opBoolean","SPLIT",EDGE,{"disambiguationData":[TD([subQ7])],"derivedFrom":makeQuery(id+"F1MoAnU7Y2teXVl_2.1.F5.boolean.opBoolean","SPLIT",EDGE,{"disambiguationData":[TD([subQ7])],"derivedFrom":makeQuery(id+"F4.opRevolve","SWEPT_EDGE",EDGE,{"disambiguationData":[OSD([subQ0,subQ2])]})})})});}
            var Q5;
            {var subQ0=sQuery(id+"F0.wireOp",EDGE,"E2");var subQ2=sQuery(id+"F0.wireOp",EDGE,"E29");var subQ4=sQuery(id+"F1.wireOp",EDGE,"E80");var subQ5=sQuery(id+"F1.wireOp",EDGE,"E79");var subQ6=makeQuery(id+"F1MoAnU7Y2teXVl_2.3.F5.opExtrude","SWEPT_FACE",FACE,{"disambiguationData":[OSD([subQ5])]});var subQ7=makeQuery(id+"F5.boolean.opBoolean","COPY",FACE,{"derivedFrom":makeQuery(id+"F5.opExtrude","SWEPT_FACE",FACE,{"disambiguationData":[OSD([subQ4])]})});Q5=makeQuery(id+"F1MoAnU7Y2teXVl_2.4.F5.boolean.opBoolean","SPLIT",EDGE,{"disambiguationData":[TD([makeQuery(id+"F1MoAnU7Y2teXVl_2.3.F5.boolean.opBoolean","COPY",FACE,{"derivedFrom":subQ6})])],"derivedFrom":makeQuery(id+"F1MoAnU7Y2teXVl_2.3.F5.boolean.opBoolean","SPLIT",EDGE,{"disambiguationData":[TD([subQ7])],"derivedFrom":makeQuery(id+"F1MoAnU7Y2teXVl_2.2.F5.boolean.opBoolean","SPLIT",EDGE,{"disambiguationData":[TD([subQ7])],"derivedFrom":makeQuery(id+"F1MoAnU7Y2teXVl_2.1.F5.boolean.opBoolean","SPLIT",EDGE,{"disambiguationData":[TD([subQ7])],"derivedFrom":makeQuery(id+"F4.opRevolve","SWEPT_EDGE",EDGE,{"disambiguationData":[OSD([subQ0,subQ2])]})})})})});}
            var Q6;
            {var subQ0=sQuery(id+"F0.wireOp",EDGE,"E2");var subQ2=sQuery(id+"F0.wireOp",EDGE,"E29");var subQ4=sQuery(id+"F1.wireOp",EDGE,"E79");var subQ5=makeQuery(id+"F1MoAnU7Y2teXVl_2.4.F5.opExtrude","SWEPT_FACE",FACE,{"disambiguationData":[OSD([subQ4])]});var subQ6=sQuery(id+"F1.wireOp",EDGE,"E80");var subQ7=makeQuery(id+"F5.boolean.opBoolean","COPY",FACE,{"derivedFrom":makeQuery(id+"F5.opExtrude","SWEPT_FACE",FACE,{"disambiguationData":[OSD([subQ6])]})});Q6=makeQuery(id+"F1MoAnU7Y2teXVl_2.5.F5.boolean.opBoolean","SPLIT",EDGE,{"disambiguationData":[TD([makeQuery(id+"F1MoAnU7Y2teXVl_2.4.F5.boolean.opBoolean","COPY",FACE,{"derivedFrom":subQ5})])],"derivedFrom":makeQuery(id+"F1MoAnU7Y2teXVl_2.4.F5.boolean.opBoolean","SPLIT",EDGE,{"disambiguationData":[TD([subQ7])],"derivedFrom":makeQuery(id+"F1MoAnU7Y2teXVl_2.3.F5.boolean.opBoolean","SPLIT",EDGE,{"disambiguationData":[TD([subQ7])],"derivedFrom":makeQuery(id+"F1MoAnU7Y2teXVl_2.2.F5.boolean.opBoolean","SPLIT",EDGE,{"disambiguationData":[TD([subQ7])],"derivedFrom":makeQuery(id+"F1MoAnU7Y2teXVl_2.1.F5.boolean.opBoolean","SPLIT",EDGE,{"disambiguationData":[TD([subQ7])],"derivedFrom":makeQuery(id+"F4.opRevolve","SWEPT_EDGE",EDGE,{"disambiguationData":[OSD([subQ0,subQ2])]})})})})})});}
            var Q7;
            {var subQ0=sQuery(id+"F0.wireOp",EDGE,"E2");var subQ2=sQuery(id+"F0.wireOp",EDGE,"E29");var subQ4=sQuery(id+"F1.wireOp",EDGE,"E79");var subQ5=makeQuery(id+"F1MoAnU7Y2teXVl_2.5.F5.opExtrude","SWEPT_FACE",FACE,{"disambiguationData":[OSD([subQ4])]});var subQ6=sQuery(id+"F1.wireOp",EDGE,"E80");var subQ7=makeQuery(id+"F5.boolean.opBoolean","COPY",FACE,{"derivedFrom":makeQuery(id+"F5.opExtrude","SWEPT_FACE",FACE,{"disambiguationData":[OSD([subQ6])]})});Q7=makeQuery(id+"F1MoAnU7Y2teXVl_2.6.F5.boolean.opBoolean","SPLIT",EDGE,{"disambiguationData":[TD([makeQuery(id+"F1MoAnU7Y2teXVl_2.5.F5.boolean.opBoolean","COPY",FACE,{"derivedFrom":subQ5})])],"derivedFrom":makeQuery(id+"F1MoAnU7Y2teXVl_2.5.F5.boolean.opBoolean","SPLIT",EDGE,{"disambiguationData":[TD([subQ7])],"derivedFrom":makeQuery(id+"F1MoAnU7Y2teXVl_2.4.F5.boolean.opBoolean","SPLIT",EDGE,{"disambiguationData":[TD([subQ7])],"derivedFrom":makeQuery(id+"F1MoAnU7Y2teXVl_2.3.F5.boolean.opBoolean","SPLIT",EDGE,{"disambiguationData":[TD([subQ7])],"derivedFrom":makeQuery(id+"F1MoAnU7Y2teXVl_2.2.F5.boolean.opBoolean","SPLIT",EDGE,{"disambiguationData":[TD([subQ7])],"derivedFrom":makeQuery(id+"F1MoAnU7Y2teXVl_2.1.F5.boolean.opBoolean","SPLIT",EDGE,{"disambiguationData":[TD([subQ7])],"derivedFrom":makeQuery(id+"F4.opRevolve","SWEPT_EDGE",EDGE,{"disambiguationData":[OSD([subQ0,subQ2])]})})})})})})});}
            var Q8;
            {var subQ0=sQuery(id+"F0.wireOp",EDGE,"E2");var subQ2=sQuery(id+"F1.wireOp",EDGE,"E80");var subQ3=sQuery(id+"F0.wireOp",EDGE,"E29");var subQ5=sQuery(id+"F1.wireOp",EDGE,"E79");var subQ6=makeQuery(id+"F1MoAnU7Y2teXVl_2.6.F5.opExtrude","SWEPT_FACE",FACE,{"disambiguationData":[OSD([subQ5])]});var subQ7=makeQuery(id+"F5.boolean.opBoolean","COPY",FACE,{"derivedFrom":makeQuery(id+"F5.opExtrude","SWEPT_FACE",FACE,{"disambiguationData":[OSD([subQ2])]})});Q8=makeQuery(id+"F1MoAnU7Y2teXVl_2.7.F5.boolean.opBoolean","SPLIT",EDGE,{"disambiguationData":[TD([makeQuery(id+"F1MoAnU7Y2teXVl_2.6.F5.boolean.opBoolean","COPY",FACE,{"derivedFrom":subQ6})])],"derivedFrom":makeQuery(id+"F1MoAnU7Y2teXVl_2.6.F5.boolean.opBoolean","SPLIT",EDGE,{"disambiguationData":[TD([subQ7])],"derivedFrom":makeQuery(id+"F1MoAnU7Y2teXVl_2.5.F5.boolean.opBoolean","SPLIT",EDGE,{"disambiguationData":[TD([subQ7])],"derivedFrom":makeQuery(id+"F1MoAnU7Y2teXVl_2.4.F5.boolean.opBoolean","SPLIT",EDGE,{"disambiguationData":[TD([subQ7])],"derivedFrom":makeQuery(id+"F1MoAnU7Y2teXVl_2.3.F5.boolean.opBoolean","SPLIT",EDGE,{"disambiguationData":[TD([subQ7])],"derivedFrom":makeQuery(id+"F1MoAnU7Y2teXVl_2.2.F5.boolean.opBoolean","SPLIT",EDGE,{"disambiguationData":[TD([subQ7])],"derivedFrom":makeQuery(id+"F1MoAnU7Y2teXVl_2.1.F5.boolean.opBoolean","SPLIT",EDGE,{"disambiguationData":[TD([subQ7])],"derivedFrom":makeQuery(id+"F4.opRevolve","SWEPT_EDGE",EDGE,{"disambiguationData":[OSD([subQ0,subQ3])]})})})})})})})});}
            var Q9;
            {var subQ0=sQuery(id+"F0.wireOp",EDGE,"E2");var subQ2=sQuery(id+"F1.wireOp",EDGE,"E79");var subQ3=makeQuery(id+"F1MoAnU7Y2teXVl_2.7.F5.opExtrude","SWEPT_FACE",FACE,{"disambiguationData":[OSD([subQ2])]});var subQ4=sQuery(id+"F0.wireOp",EDGE,"E29");var subQ6=sQuery(id+"F1.wireOp",EDGE,"E80");var subQ7=makeQuery(id+"F5.boolean.opBoolean","COPY",FACE,{"derivedFrom":makeQuery(id+"F5.opExtrude","SWEPT_FACE",FACE,{"disambiguationData":[OSD([subQ6])]})});Q9=makeQuery(id+"F1MoAnU7Y2teXVl_2.8.F5.boolean.opBoolean","SPLIT",EDGE,{"disambiguationData":[TD([makeQuery(id+"F1MoAnU7Y2teXVl_2.7.F5.boolean.opBoolean","COPY",FACE,{"derivedFrom":subQ3})])],"derivedFrom":makeQuery(id+"F1MoAnU7Y2teXVl_2.7.F5.boolean.opBoolean","SPLIT",EDGE,{"disambiguationData":[TD([subQ7])],"derivedFrom":makeQuery(id+"F1MoAnU7Y2teXVl_2.6.F5.boolean.opBoolean","SPLIT",EDGE,{"disambiguationData":[TD([subQ7])],"derivedFrom":makeQuery(id+"F1MoAnU7Y2teXVl_2.5.F5.boolean.opBoolean","SPLIT",EDGE,{"disambiguationData":[TD([subQ7])],"derivedFrom":makeQuery(id+"F1MoAnU7Y2teXVl_2.4.F5.boolean.opBoolean","SPLIT",EDGE,{"disambiguationData":[TD([subQ7])],"derivedFrom":makeQuery(id+"F1MoAnU7Y2teXVl_2.3.F5.boolean.opBoolean","SPLIT",EDGE,{"disambiguationData":[TD([subQ7])],"derivedFrom":makeQuery(id+"F1MoAnU7Y2teXVl_2.2.F5.boolean.opBoolean","SPLIT",EDGE,{"disambiguationData":[TD([subQ7])],"derivedFrom":makeQuery(id+"F1MoAnU7Y2teXVl_2.1.F5.boolean.opBoolean","SPLIT",EDGE,{"disambiguationData":[TD([subQ7])],"derivedFrom":makeQuery(id+"F4.opRevolve","SWEPT_EDGE",EDGE,{"disambiguationData":[OSD([subQ0,subQ4])]})})})})})})})})});}
            fillet(context, id + "F7", {"entities" : qUnion([Q0, Q1, Q2, Q3, Q4, Q5, Q6, Q7, Q8, Q9]), "radius" : 5 * mm, "tangentPropagation" : true, "allowEdgeOverflow" : false});
        }
        {
            var Q0;
            Q0=makeQuery(id+"F0.imprint","IMPRINT",FACE,{"disambiguationData":[TD([[makeQuery(id+"F0.imprint","IMPRINT",EDGE,{"derivedFrom":sQuery(id+"F0.wireOp",EDGE,"E21.0")}),1.0]])]});
            var Q1;
            {var subQ0=sQuery(id+"F0.wireOp",EDGE,"bqb2CW3f-qtDE-810B-vVhX-ZT2S4oLEjpGb");Q1=makeQuery(id+"F0.imprint","IMPRINT",FACE,{"disambiguationData":[TD([[makeQuery(id+"F0.imprint","IMPRINT",EDGE,{"derivedFrom":subQ0}),1.0]])]});}
            var Q2;
            Q2=sQuery(id+"F0.wireOp",EDGE,"E28");
            revolve(context, id + "F8", {"entities" : qUnion([Q0, Q1]), "axis" : qUnion([Q2]), "revolveType" : RevolveType.FULL});
        }
        {
            var Q0;
            Q0=makeQuery(id+"F0.imprint","IMPRINT",FACE,{"disambiguationData":[TD([[makeQuery(id+"F0.imprint","IMPRINT",EDGE,{"derivedFrom":sQuery(id+"F0.wireOp",EDGE,"E46")}),1.0]])]});
            var Q1;
            Q1=sQuery(id+"F0.wireOp",EDGE,"E28");
            revolve(context, id + "F9", {"entities" : qUnion([Q0]), "axis" : qUnion([Q1]), "revolveType" : RevolveType.FULL});
        }
        {
            var Q0;
            Q0=makeQuery(id+"F2.imprint","IMPRINT",FACE,{"disambiguationData":[TD([[makeQuery(id+"F2.imprint","IMPRINT",EDGE,{"derivedFrom":sQuery(id+"F2.wireOp",EDGE,"E83")}),-1.0]])]});
            extrude(context, id + "F10", {"entities" : qUnion([Q0]), "operationType" : NewBodyOperationType.INTERSECT, "endBound" : BoundingType.THROUGH_ALL, "oppositeDirection" : true, "depth" : 300 * mm});
        }
    });
